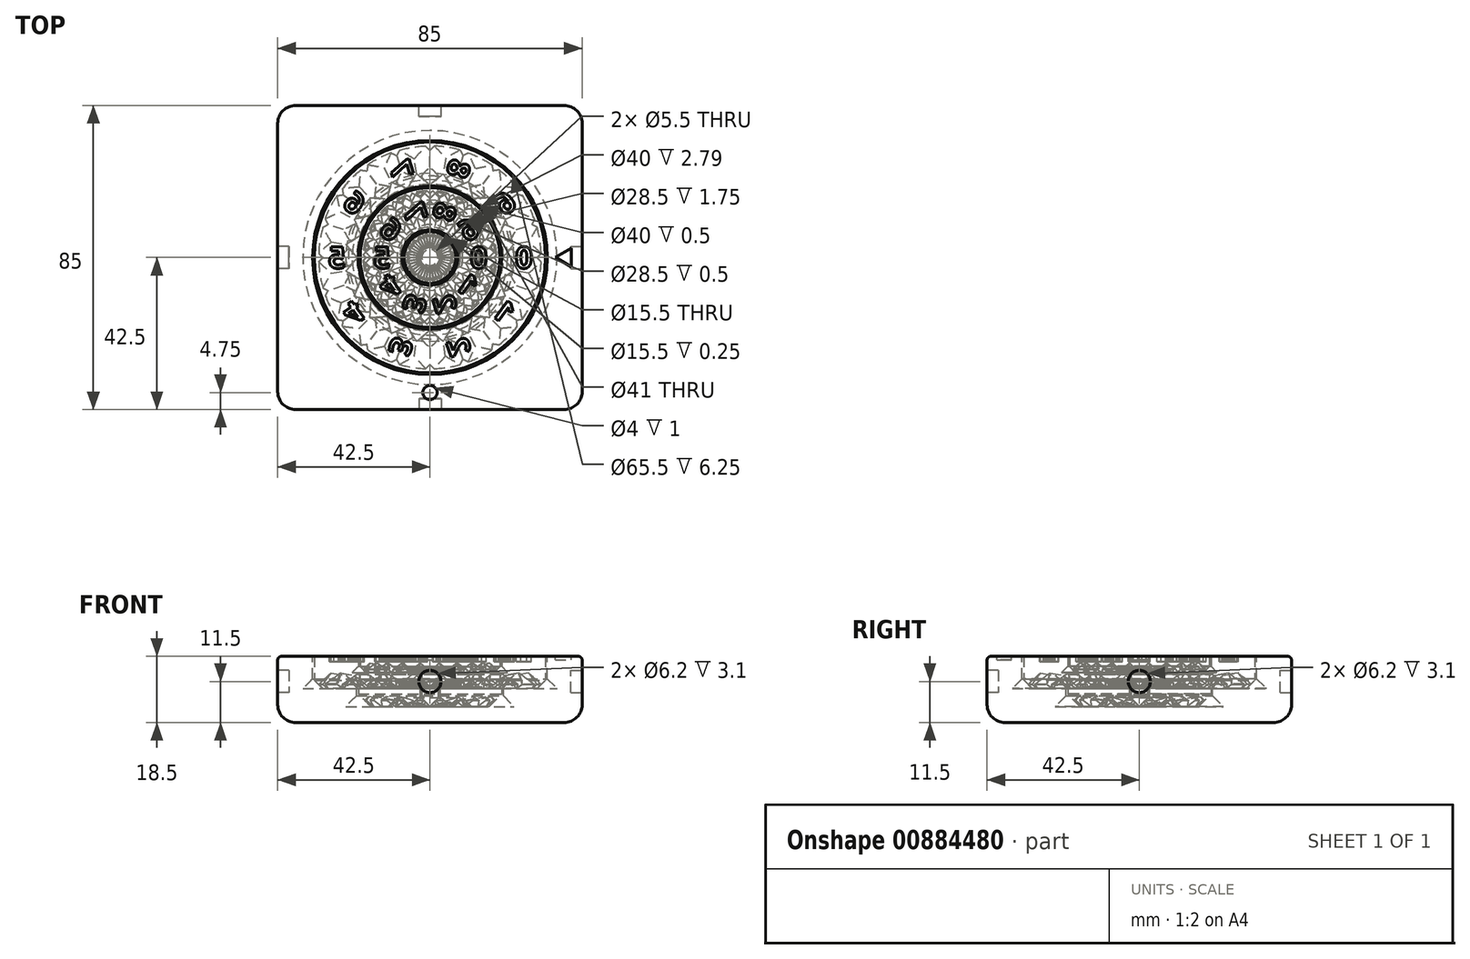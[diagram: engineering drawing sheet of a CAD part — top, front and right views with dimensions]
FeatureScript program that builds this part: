
annotation { "Feature Type Name" : "Feature", "Feature Type Description" : "" }
export const myFeature = defineFeature(function(context is Context, id is Id, definition is map)
    precondition{}
    {
        {
            var Q0;
            Q0=qCreatedBy(makeId("Top.planeOp"),FACE);
            var sketch = newSketch(context, id + "F0", { "sketchPlane" : qUnion([Q0])});
            skLineSegment(sketch, "E0.bottom", {"start": v(-42.5, 42.5) * mm, "end": v(42.5, 42.5) * mm});
            skLineSegment(sketch, "E0.top", {"start": v(-42.5, -42.5) * mm, "end": v(42.5, -42.5) * mm});
            skLineSegment(sketch, "E0.left", {"start": v(-42.5, 42.5) * mm, "end": v(-42.5, -42.5) * mm});
            skLineSegment(sketch, "E0.right", {"start": v(42.5, 42.5) * mm, "end": v(42.5, -42.5) * mm});
            skLineSegment(sketch, "E1", {"start": v(-42.5, 0) * mm, "end": v(42.5, 0) * mm, "construction": true});
            skLineSegment(sketch, "E2", {"start": v(0, -42.5) * mm, "end": v(0, 42.5) * mm, "construction": true});
            skCircle(sketch, "E3", {"center": v(0, -37.75) * mm, "radius": 2 * mm});
            skCircle(sketch, "E4", {"center": v(0, 0) * mm, "radius": 32.75 * mm});
            skCircle(sketch, "E5", {"center": v(0, 0) * mm, "radius": 20.5 * mm});
            skSolve(sketch);
        }
        {
            assignVariable(context, id + "F1", {"name" : "h", "anyValue" : 18.5});
        }
        {
            assignVariable(context, id + "F2", {"name" : "d", "anyValue" : 14});
        }
        {
            var Q0;
            Q0=makeQuery(id+"F0.imprint","IMPRINT",FACE,{"disambiguationData":[TD([[makeQuery(id+"F0.imprint","IMPRINT",EDGE,{"derivedFrom":sQuery(id+"F0.wireOp",EDGE,"TAnjNuv1-8zZz-IdIO-9YnW-rZbYslCo22iK.bottom")}),-1.0]])]});
            var Q1;
            Q1=makeQuery(id+"F0.imprint","IMPRINT",FACE,{"disambiguationData":[TD([[makeQuery(id+"F0.imprint","IMPRINT",EDGE,{"derivedFrom":sQuery(id+"F0.wireOp",EDGE,"E0.bottom")}),-1.0]])]});
            var Q2;
            Q2=makeQuery(id+"F0.imprint","IMPRINT",FACE,{"disambiguationData":[TD([[makeQuery(id+"F0.imprint","IMPRINT",EDGE,{"derivedFrom":sQuery(id+"F0.wireOp",EDGE,"2ee7e992-b2ee-4d81-b33c-59d4d4482344.0.2.0")}),1.0]])]});
            var Q3;
            Q3=makeQuery(id+"F0.imprint","IMPRINT",FACE,{"disambiguationData":[TD([[makeQuery(id+"F0.imprint","IMPRINT",EDGE,{"derivedFrom":sQuery(id+"F0.wireOp",EDGE,"2ee7e992-b2ee-4d81-b33c-59d4d4482344.0.3.0")}),1.0]])]});
            var Q4;
            Q4=makeQuery(id+"F0.imprint","IMPRINT",FACE,{"disambiguationData":[TD([[makeQuery(id+"F0.imprint","IMPRINT",EDGE,{"derivedFrom":sQuery(id+"F0.wireOp",EDGE,"2ee7e992-b2ee-4d81-b33c-59d4d4482344.0.1.0")}),1.0]])]});
            var Q5;
            Q5=makeQuery(id+"F0.imprint","IMPRINT",FACE,{"disambiguationData":[TD([[makeQuery(id+"F0.imprint","IMPRINT",EDGE,{"derivedFrom":sQuery(id+"F0.wireOp",EDGE,"f406dc69-17c4-4892-9ae8-b8d3958ef0eb.0.1.2")}),1.0]])]});
            var Q6;
            Q6=makeQuery(id+"F0.imprint","IMPRINT",FACE,{"disambiguationData":[TD([[makeQuery(id+"F0.imprint","IMPRINT",EDGE,{"derivedFrom":sQuery(id+"F0.wireOp",EDGE,"f406dc69-17c4-4892-9ae8-b8d3958ef0eb.0.2.2")}),1.0]])]});
            var Q7;
            Q7=makeQuery(id+"F0.imprint","IMPRINT",FACE,{"disambiguationData":[TD([[makeQuery(id+"F0.imprint","IMPRINT",EDGE,{"derivedFrom":sQuery(id+"F0.wireOp",EDGE,"f406dc69-17c4-4892-9ae8-b8d3958ef0eb.0.3.2")}),1.0]])]});
            var Q8;
            Q8=makeQuery(id+"F0.imprint","IMPRINT",FACE,{"disambiguationData":[TD([[makeQuery(id+"F0.imprint","IMPRINT",EDGE,{"derivedFrom":sQuery(id+"F0.wireOp",EDGE,"E3")}),1.0]])]});
            var Q9;
            Q9=makeQuery(id+"F0.imprint","IMPRINT",FACE,{"disambiguationData":[TD([[makeQuery(id+"F0.imprint","IMPRINT",EDGE,{"derivedFrom":sQuery(id+"F0.wireOp",EDGE,"E4")}),1.0]])]});
            var Q10;
            Q10=makeQuery(id+"F0.imprint","IMPRINT",FACE,{"disambiguationData":[TD([[makeQuery(id+"F0.imprint","IMPRINT",EDGE,{"derivedFrom":sQuery(id+"F0.wireOp",EDGE,"E5")}),1.0]])]});
            extrude(context, id + "F3", {"entities" : qUnion([Q0, Q1, Q2, Q3, Q4, Q5, Q6, Q7, Q8, Q9, Q10]), "depth" : (getVariable(context, 'h')) * mm, "offsetDistance" : 25 * mm});
        }
        {
            var Q0;
            Q0=makeQuery(id+"F0.imprint","IMPRINT",FACE,{"disambiguationData":[TD([[makeQuery(id+"F0.imprint","IMPRINT",EDGE,{"derivedFrom":sQuery(id+"F0.wireOp",EDGE,"E4")}),1.0]])]});
            extrude(context, id + "F4", {"entities" : qUnion([Q0]), "operationType" : NewBodyOperationType.REMOVE, "depth" : (getVariable(context, 'd') - 5) * mm, "offsetDistance" : 25 * mm});
        }
        {
            var Q0;
            Q0=makeQuery(id+"F0.imprint","IMPRINT",FACE,{"disambiguationData":[TD([[makeQuery(id+"F0.imprint","IMPRINT",EDGE,{"derivedFrom":sQuery(id+"F0.wireOp",EDGE,"E5")}),1.0]])]});
            extrude(context, id + "F5", {"entities" : qUnion([Q0]), "operationType" : NewBodyOperationType.REMOVE, "depth" : (getVariable(context, 'd')) * mm, "offsetDistance" : 25 * mm});
        }
        {
            var Q0;
            Q0=makeQuery(id+"F3.opExtrude","CAP_FACE",FACE,{"disambiguationData":[OSD([sQuery(id+"F0.wireOp",EDGE,"E0.bottom"),sQuery(id+"F0.wireOp",EDGE,"E0.top"),sQuery(id+"F0.wireOp",EDGE,"E0.left"),sQuery(id+"F0.wireOp",EDGE,"E0.right")])],"isStart":false});
            var Q1;
            Q1=makeQuery(id+"F3.opExtrude","SWEPT_EDGE",EDGE,{"disambiguationData":[OSD([sQuery(id+"F0.wireOp",EDGE,"E0.bottom"),sQuery(id+"F0.wireOp",EDGE,"E0.right")])]});
            var Q2;
            Q2=makeQuery(id+"F3.opExtrude","SWEPT_EDGE",EDGE,{"disambiguationData":[OSD([sQuery(id+"F0.wireOp",EDGE,"E0.bottom"),sQuery(id+"F0.wireOp",EDGE,"E0.left")])]});
            var Q3;
            Q3=makeQuery(id+"F3.opExtrude","SWEPT_EDGE",EDGE,{"disambiguationData":[OSD([sQuery(id+"F0.wireOp",EDGE,"E0.top"),sQuery(id+"F0.wireOp",EDGE,"E0.left")])]});
            var Q4;
            Q4=makeQuery(id+"F3.opExtrude","SWEPT_EDGE",EDGE,{"disambiguationData":[OSD([sQuery(id+"F0.wireOp",EDGE,"E0.top"),sQuery(id+"F0.wireOp",EDGE,"E0.right")])]});
            fillet(context, id + "F6", {"entities" : qUnion([Q0, Q1, Q2, Q3, Q4]), "radius" : 5 * mm, "tangentPropagation" : true, "allowEdgeOverflow" : false});
        }
        {
            var Q0;
            Q0=makeQuery(id+"F3.opExtrude","CAP_EDGE",EDGE,{"disambiguationData":[OSD([sQuery(id+"F0.wireOp",EDGE,"E0.left")])],"isStart":true});
            fillet(context, id + "F7", {"entities" : qUnion([Q0]), "radius" : 1 * mm, "tangentPropagation" : true, "allowEdgeOverflow" : false});
        }
        {
            var Q0;
            Q0=makeQuery(id+"F3.opExtrude","SWEPT_FACE",FACE,{"disambiguationData":[OSD([sQuery(id+"F0.wireOp",EDGE,"E0.top")])]});
            var sketch = newSketch(context, id + "F8", { "sketchPlane" : qUnion([Q0])});
            skCircle(sketch, "E6", {"center": v(0, 7) * mm, "radius": 3.1 * mm});
            skSolve(sketch);
        }
        {
            var Q0;
            Q0=makeQuery(id+"F8.imprint","IMPRINT",FACE,{"disambiguationData":[TD([[makeQuery(id+"F8.imprint","IMPRINT",EDGE,{"derivedFrom":sQuery(id+"F8.wireOp",EDGE,"E6")}),1.0]])]});
            extrude(context, id + "F9", {"entities" : qUnion([Q0]), "operationType" : NewBodyOperationType.REMOVE, "oppositeDirection" : true, "depth" : 3.1 * mm, "offsetDistance" : 25 * mm});
        }
        {
            var Q0;
            Q0=makeQuery(id+"F3.opExtrude","SWEPT_FACE",FACE,{"disambiguationData":[OSD([sQuery(id+"F0.wireOp",EDGE,"E0.bottom")])]});
            var sketch = newSketch(context, id + "F10", { "sketchPlane" : qUnion([Q0])});
            skCircle(sketch, "E7", {"center": v(0, 7) * mm, "radius": 3.1 * mm});
            skSolve(sketch);
        }
        {
            var Q0;
            Q0=makeQuery(id+"F10.imprint","IMPRINT",FACE,{"disambiguationData":[TD([[makeQuery(id+"F10.imprint","IMPRINT",EDGE,{"derivedFrom":sQuery(id+"F10.wireOp",EDGE,"E7")}),1.0]])]});
            extrude(context, id + "F11", {"entities" : qUnion([Q0]), "operationType" : NewBodyOperationType.REMOVE, "oppositeDirection" : true, "depth" : 3.1 * mm, "offsetDistance" : 25 * mm});
        }
        {
            var Q0;
            Q0=makeQuery(id+"F3.opExtrude","SWEPT_FACE",FACE,{"disambiguationData":[OSD([sQuery(id+"F0.wireOp",EDGE,"E0.left")])]});
            var sketch = newSketch(context, id + "F12", { "sketchPlane" : qUnion([Q0])});
            skCircle(sketch, "E8", {"center": v(0, 7) * mm, "radius": 3.1 * mm});
            skSolve(sketch);
        }
        {
            var Q0;
            Q0=makeQuery(id+"F12.imprint","IMPRINT",FACE,{"disambiguationData":[TD([[makeQuery(id+"F12.imprint","IMPRINT",EDGE,{"derivedFrom":sQuery(id+"F12.wireOp",EDGE,"E8")}),1.0]])]});
            extrude(context, id + "F13", {"entities" : qUnion([Q0]), "operationType" : NewBodyOperationType.REMOVE, "oppositeDirection" : true, "depth" : 3.1 * mm, "offsetDistance" : 25 * mm});
        }
        {
            var Q0;
            Q0=makeQuery(id+"F3.opExtrude","SWEPT_FACE",FACE,{"disambiguationData":[OSD([sQuery(id+"F0.wireOp",EDGE,"E0.right")])]});
            var sketch = newSketch(context, id + "F14", { "sketchPlane" : qUnion([Q0])});
            skCircle(sketch, "E9", {"center": v(0, 7) * mm, "radius": 3.1 * mm});
            skSolve(sketch);
        }
        {
            var Q0;
            Q0=makeQuery(id+"F14.imprint","IMPRINT",FACE,{"disambiguationData":[TD([[makeQuery(id+"F14.imprint","IMPRINT",EDGE,{"derivedFrom":sQuery(id+"F14.wireOp",EDGE,"E9")}),1.0]])]});
            extrude(context, id + "F15", {"entities" : qUnion([Q0]), "operationType" : NewBodyOperationType.REMOVE, "oppositeDirection" : true, "depth" : 3.1 * mm, "offsetDistance" : 25 * mm});
        }
        {
            var Q0;
            Q0=makeQuery(id+"F0.imprint","IMPRINT",FACE,{"disambiguationData":[TD([[makeQuery(id+"F0.imprint","IMPRINT",EDGE,{"derivedFrom":sQuery(id+"F0.wireOp",EDGE,"E3")}),1.0]])]});
            var Q1;
            Q1=sQuery(id+"F0.wireOp",EDGE,"E3");
            extrude(context, id + "F16", {"entities" : qUnion([Q0]), "operationType" : NewBodyOperationType.REMOVE, "surfaceEntities" : qUnion([Q1]), "depth" : 1 * mm, "offsetDistance" : 25 * mm});
        }
        {
            var Q0;
            Q0=qCreatedBy(makeId("Front.planeOp"),FACE);
            var sketch = newSketch(context, id + "F17", { "sketchPlane" : qUnion([Q0])});
            skLineSegment(sketch, "E10", {"start": v(0, 14) * mm, "end": v(0, 9) * mm, "construction": true});
            skLineSegment(sketch, "E11", {"start": v(-20, 0) * mm, "end": v(-32.25, 0) * mm});
            skLineSegment(sketch, "E12", {"start": v(-32.25, 0) * mm, "end": v(-32.25, 9) * mm});
            skLineSegment(sketch, "E13", {"start": v(-32.25, 9) * mm, "end": v(-20, 9) * mm});
            skLineSegment(sketch, "E14", {"start": v(-20, 9) * mm, "end": v(-20, 14) * mm});
            skLineSegment(sketch, "E15", {"start": v(-20, 14) * mm, "end": v(-2.75, 14) * mm});
            skPoint(sketch, "E16.visualSharp", {"position": v(-20, 14) * mm});
            skPoint(sketch, "E17.visualSharp", {"position": v(-32.25, 9) * mm});
            skPoint(sketch, "E18.visualSharp", {"position": v(-20, 9) * mm});
            skPoint(sketch, "E19.orphan", {"position": v(0, 28.15) * mm});
            skLineSegment(sketch, "E20", {"start": v(-20, 0) * mm, "end": v(-20, 5) * mm});
            skLineSegment(sketch, "E21", {"start": v(-20, 5) * mm, "end": v(-14.25, 5) * mm});
            skLineSegment(sketch, "E22", {"start": v(-14.25, 5) * mm, "end": v(-14.25, 9) * mm});
            skLineSegment(sketch, "E23", {"start": v(-14.25, 9) * mm, "end": v(-2.75, 9) * mm});
            skPoint(sketch, "E24.visualSharp", {"position": v(-14.25, 9) * mm});
            skPoint(sketch, "E25.visualSharp", {"position": v(-14.25, 5) * mm});
            skPoint(sketch, "E26.visualSharp", {"position": v(-20, 5) * mm});
            skLineSegment(sketch, "E27", {"start": v(-2.75, 14) * mm, "end": v(-2.75, 9) * mm});
            skSolve(sketch);
        }
        {
            var Q0;
            Q0=makeQuery(id+"F17.imprint","IMPRINT",FACE,{"disambiguationData":[TD([[makeQuery(id+"F17.imprint","IMPRINT",EDGE,{"derivedFrom":sQuery(id+"F17.wireOp",EDGE,"E11")}),-1.0]])]});
            var Q1;
            Q1 = qConstructionFilter(qBodyType(qCreatedBy(id + "F17" ,EDGE), BodyType.WIRE), ConstructionObject.NO);
            var Q2;
            Q2=sQuery(id+"F17.wireOp",EDGE,"E10");
            revolve(context, id + "F18", {"surfaceOperationType" : NewSurfaceOperationType.NEW, "entities" : qUnion([Q0]), "surfaceEntities" : qUnion([Q1]), "axis" : qUnion([Q2]), "revolveType" : RevolveType.FULL});
        }
        {
            var Q0;
            Q0=qCreatedBy(makeId("Front.planeOp"),FACE);
            var sketch = newSketch(context, id + "F19", { "sketchPlane" : qUnion([Q0])});
            skLineSegment(sketch, "E28", {"start": v(-2.75, 8.5) * mm, "end": v(-13.75, 8.5) * mm});
            skLineSegment(sketch, "E29", {"start": v(-13.75, 8.5) * mm, "end": v(-13.75, 4.5) * mm});
            skLineSegment(sketch, "E30", {"start": v(-13.75, 4.5) * mm, "end": v(-19.5, 4.5) * mm});
            skLineSegment(sketch, "E31", {"start": v(-19.5, 4.5) * mm, "end": v(-19.5, 0) * mm});
            skLineSegment(sketch, "E32", {"start": v(-19.5, 0) * mm, "end": v(-7.75, 0) * mm});
            skLineSegment(sketch, "E33", {"start": v(-7.75, 0) * mm, "end": v(-7.75, 4.5) * mm});
            skLineSegment(sketch, "E34", {"start": v(-7.75, 4.5) * mm, "end": v(-2.75, 4.5) * mm});
            skLineSegment(sketch, "E35", {"start": v(-2.75, 4.5) * mm, "end": v(-2.75, 8.5) * mm});
            skPoint(sketch, "E36.orphan", {"position": v(0, 8.5) * mm});
            skLineSegment(sketch, "E37", {"start": v(0, 19.44) * mm, "end": v(0, -7.38) * mm, "construction": true});
            skSolve(sketch);
        }
        {
            var Q0;
            Q0=makeQuery(id+"F19.imprint","IMPRINT",FACE,{"disambiguationData":[TD([[makeQuery(id+"F19.imprint","IMPRINT",EDGE,{"derivedFrom":sQuery(id+"F19.wireOp",EDGE,"E28")}),1.0]])]});
            var Q1;
            Q1=sQuery(id+"F19.wireOp",EDGE,"E37");
            revolve(context, id + "F20", {"surfaceOperationType" : NewSurfaceOperationType.NEW, "entities" : qUnion([Q0]), "axis" : qUnion([Q1]), "revolveType" : RevolveType.FULL});
        }
        {
            var Q0;
            Q0=makeQuery(id+"F0.imprint","IMPRINT",FACE,{"disambiguationData":[TD([[makeQuery(id+"F0.imprint","IMPRINT",EDGE,{"derivedFrom":sQuery(id+"F0.wireOp",EDGE,"E0.bottom")}),-1.0]])]});
            var sketch = newSketch(context, id + "F21", { "sketchPlane" : qUnion([Q0])});
            skLineSegment(sketch, "E38", {"start": v(0, 0) * mm, "end": v(13.5, 0) * mm, "construction": true});
            skLineSegment(sketch, "E39.1.0", {"start": v(0, 0) * mm, "end": v(32.76, 23.8) * mm, "construction": true});
            skLineSegment(sketch, "E39.2.0", {"start": v(0, 0) * mm, "end": v(12.51, 38.5) * mm, "construction": true});
            skLineSegment(sketch, "E39.3.0", {"start": v(0, 0) * mm, "end": v(-12.51, 38.5) * mm, "construction": true});
            skLineSegment(sketch, "E39.4.0", {"start": v(0, 0) * mm, "end": v(-32.76, 23.8) * mm, "construction": true});
            skLineSegment(sketch, "E39.5.0", {"start": v(0, 0) * mm, "end": v(-13.5, 0) * mm, "construction": true});
            skLineSegment(sketch, "E39.6.0", {"start": v(0, 0) * mm, "end": v(-21.14, -15.36) * mm, "construction": true});
            skLineSegment(sketch, "E39.7.0", {"start": v(0, 0) * mm, "end": v(-12.51, -38.5) * mm, "construction": true});
            skLineSegment(sketch, "E39.8.0", {"start": v(0, 0) * mm, "end": v(8.07, -24.85) * mm, "construction": true});
            skLineSegment(sketch, "E39.9.0", {"start": v(0, 0) * mm, "end": v(21.14, -15.36) * mm, "construction": true});
            skPoint(sketch, "E39.center", {"position": v(0, 0) * mm});
            skCircle(sketch, "E40", {"center": v(0, 0) * mm, "radius": 32.5 * mm, "construction": true});
            skCircle(sketch, "E41", {"center": v(0, 0) * mm, "radius": 19.75 * mm, "construction": true});
            skText(sketch, "E42", { "text": "0", "fontName": "OpenSans-Bold.ttf"});
            skLineSegment(sketch, "E43", {"start": v(-26.12, 0) * mm, "end": v(-28.62, 0) * mm, "construction": true});
            skLineSegment(sketch, "E44", {"start": v(-21.14, -15.36) * mm, "end": v(-32.76, -23.8) * mm, "construction": true});
            skArc(sketch, "E45", {"start": v(-21.14, 15.36) * mm, "mid": v(-24.85, -8.07) * mm, "end": v(-8.07, -24.85) * mm, "construction": true});
            skArc(sketch, "E46", {"start": v(-8.07, 24.85) * mm, "mid": v(-15.36, 21.14) * mm, "end": v(-21.14, 15.36) * mm, "construction": true});
            skArc(sketch, "E47", {"start": v(8.07, 24.85) * mm, "mid": v(0, 26.12) * mm, "end": v(-8.07, 24.85) * mm, "construction": true});
            skArc(sketch, "E48", {"start": v(21.14, 15.36) * mm, "mid": v(15.36, 21.14) * mm, "end": v(8.07, 24.85) * mm, "construction": true});
            skArc(sketch, "E49", {"start": v(26.12, 0) * mm, "mid": v(24.85, 8.07) * mm, "end": v(21.14, 15.36) * mm, "construction": true});
            skLineSegment(sketch, "E50", {"start": v(21.14, -15.36) * mm, "end": v(32.76, -23.8) * mm, "construction": true});
            skLineSegment(sketch, "E51", {"start": v(8.07, -24.85) * mm, "end": v(12.51, -38.5) * mm, "construction": true});
            skArc(sketch, "E52", {"start": v(-8.07, -24.85) * mm, "mid": v(15.36, -21.14) * mm, "end": v(26.12, 0) * mm, "construction": true});
            skText(sketch, "E53", { "text": "1", "fontName": "OpenSans-Bold.ttf"});
            skLineSegment(sketch, "E54", {"start": v(-21.14, -15.36) * mm, "end": v(-22.75, -16.53) * mm, "construction": true});
            skText(sketch, "E55", { "text": "2", "fontName": "OpenSans-Bold.ttf"});
            skLineSegment(sketch, "E56", {"start": v(-8.07, -24.85) * mm, "end": v(-8.85, -27.24) * mm, "construction": true});
            skText(sketch, "E57", { "text": "3", "fontName": "OpenSans-Bold.ttf"});
            skLineSegment(sketch, "E58", {"start": v(8.07, -24.85) * mm, "end": v(8.84, -27.21) * mm, "construction": true});
            skText(sketch, "E59", { "text": "4", "fontName": "OpenSans-Bold.ttf"});
            skLineSegment(sketch, "E60", {"start": v(23.23, -16.87) * mm, "end": v(21.14, -15.36) * mm, "construction": true});
            skText(sketch, "E61", { "text": "5\n", "fontName": "OpenSans-Bold.ttf"});
            skLineSegment(sketch, "E62", {"start": v(26.13, 0) * mm, "end": v(23.66, 0) * mm, "construction": true});
            skText(sketch, "E63", { "text": "6\n", "fontName": "OpenSans-Bold.ttf"});
            skLineSegment(sketch, "E64", {"start": v(21.14, 15.36) * mm, "end": v(23.17, 16.83) * mm, "construction": true});
            skText(sketch, "E65", { "text": "7", "fontName": "OpenSans-Bold.ttf"});
            skLineSegment(sketch, "E66", {"start": v(8.07, 24.85) * mm, "end": v(8.85, 27.24) * mm, "construction": true});
            skText(sketch, "E67", { "text": "8", "fontName": "OpenSans-Bold.ttf"});
            skLineSegment(sketch, "E68", {"start": v(-8.85, 27.23) * mm, "end": v(-8.07, 24.85) * mm, "construction": true});
            skText(sketch, "E69", { "text": "9", "fontName": "OpenSans-Bold.ttf"});
            skLineSegment(sketch, "E70", {"start": v(-23.16, 16.83) * mm, "end": v(-21.14, 15.36) * mm, "construction": true});
            skText(sketch, "E71", { "text": "5\n", "fontName": "OpenSans-Bold.ttf"});
            skLineSegment(sketch, "E72", {"start": v(13.5, 0) * mm, "end": v(11.04, 0) * mm, "construction": true});
            skCircle(sketch, "E73", {"center": v(0, 0) * mm, "radius": 7.5 * mm, "construction": true});
            skCircle(sketch, "E74", {"center": v(0, 0) * mm, "radius": 19.5 * mm, "construction": true});
            skLineSegment(sketch, "E75", {"start": v(13.5, 0) * mm, "end": v(40.49, 0) * mm, "construction": true});
            skArc(sketch, "E76", {"start": v(10.92, 7.94) * mm, "mid": v(7.94, 10.92) * mm, "end": v(4.17, 12.84) * mm, "construction": true});
            skArc(sketch, "E77", {"start": v(10.92, -7.94) * mm, "mid": v(13.5, 0) * mm, "end": v(10.92, 7.94) * mm, "construction": true});
            skArc(sketch, "E78", {"start": v(4.17, -12.84) * mm, "mid": v(7.94, -10.92) * mm, "end": v(10.92, -7.94) * mm, "construction": true});
            skArc(sketch, "E79", {"start": v(-4.17, -12.84) * mm, "mid": v(0, -13.5) * mm, "end": v(4.17, -12.84) * mm, "construction": true});
            skArc(sketch, "E80", {"start": v(4.17, 12.84) * mm, "mid": v(0, 13.5) * mm, "end": v(-4.17, 12.84) * mm, "construction": true});
            skArc(sketch, "E81", {"start": v(-4.17, 12.84) * mm, "mid": v(-7.94, 10.92) * mm, "end": v(-10.92, 7.94) * mm, "construction": true});
            skArc(sketch, "E82", {"start": v(-10.92, 7.94) * mm, "mid": v(-13.5, 0) * mm, "end": v(-10.92, -7.94) * mm, "construction": true});
            skLineSegment(sketch, "E83", {"start": v(-13.5, 0) * mm, "end": v(-40.49, 0) * mm, "construction": true});
            skArc(sketch, "E84", {"start": v(-10.92, -7.94) * mm, "mid": v(-7.94, -10.92) * mm, "end": v(-4.17, -12.84) * mm, "construction": true});
            skText(sketch, "E85", { "text": "6\n", "fontName": "OpenSans-Bold.ttf"});
            skLineSegment(sketch, "E86", {"start": v(10.92, 7.94) * mm, "end": v(12.96, 9.41) * mm, "construction": true});
            skText(sketch, "E87", { "text": "7", "fontName": "OpenSans-Bold.ttf"});
            skLineSegment(sketch, "E88", {"start": v(4.17, 12.84) * mm, "end": v(4.95, 15.23) * mm, "construction": true});
            skText(sketch, "E89", { "text": "8", "fontName": "OpenSans-Bold.ttf"});
            skLineSegment(sketch, "E90", {"start": v(-4.95, 15.22) * mm, "end": v(-4.17, 12.84) * mm, "construction": true});
            skText(sketch, "E91", { "text": "9", "fontName": "OpenSans-Bold.ttf"});
            skLineSegment(sketch, "E92", {"start": v(-12.95, 9.4) * mm, "end": v(-10.92, 7.94) * mm, "construction": true});
            skText(sketch, "E93", { "text": "0", "fontName": "OpenSans-Bold.ttf"});
            skLineSegment(sketch, "E94", {"start": v(-13.5, 0) * mm, "end": v(-16, 0) * mm, "construction": true});
            skText(sketch, "E95", { "text": "1", "fontName": "OpenSans-Bold.ttf"});
            skLineSegment(sketch, "E96", {"start": v(-10.92, -7.94) * mm, "end": v(-12.53, -9.1) * mm, "construction": true});
            skText(sketch, "E97", { "text": "2", "fontName": "OpenSans-Bold.ttf"});
            skLineSegment(sketch, "E98", {"start": v(-4.17, -12.84) * mm, "end": v(-4.95, -15.23) * mm, "construction": true});
            skText(sketch, "E99", { "text": "3", "fontName": "OpenSans-Bold.ttf"});
            skLineSegment(sketch, "E100", {"start": v(4.17, -12.84) * mm, "end": v(4.94, -15.2) * mm, "construction": true});
            skText(sketch, "E101", { "text": "4", "fontName": "OpenSans-Bold.ttf"});
            skLineSegment(sketch, "E102", {"start": v(13.01, -9.45) * mm, "end": v(10.92, -7.94) * mm, "construction": true});
            const initialGuessF21  = {"E42": [-0.02862, -0.003, 1, 0, 0.006], "E53": [-0.02098, -0.01895, 0.80902, 0.58779, 0.006], "E55": [-0.006, -0.02817, 0.30902, 0.95106, 0.006], "E57": [0.0117, -0.02629, -0.30902, 0.95106, 0.006], "E59": [0.02499, -0.01445, -0.80902, 0.58779, 0.006], "E61": [0.02366, -0.003, 1, 0, 0.006], "E63": [0.02086, 0.01145, 0.80902, 0.58779, 0.006], "E65": [0.01015, 0.02153, 0.30902, 0.95106, 0.006], "E67": [-0.00445, 0.0234, -0.30902, 0.95106, 0.006], "E69": [-0.01735, 0.01631, -0.80902, 0.58779, 0.006], "E71": [0.01104, -0.003, 1, 0, 0.006], "E85": [0.01065, 0.00403, 0.80902, 0.58779, 0.006], "E87": [0.00625, 0.00952, 0.30902, 0.95106, 0.006], "E89": [-0.00054, 0.01138, -0.30902, 0.95106, 0.006], "E91": [-0.00713, 0.0089, -0.80902, 0.58779, 0.006], "E93": [-0.016, -0.003, 1, 0, 0.006], "E95": [-0.01077, -0.01153, 0.80902, 0.58779, 0.006], "E97": [-0.0021, -0.01616, 0.30902, 0.95106, 0.006], "E99": [0.0078, -0.01428, -0.30902, 0.95106, 0.006], "E101": [0.01478, -0.00703, -0.80902, 0.58779, 0.006]};
            skSetInitialGuess(sketch, initialGuessF21);
            skSolve(sketch);
        }
        {
            var Q0;
            Q0 = qSketchRegion(id + "F21", true);
            extrude(context, id + "F22", {"entities" : qUnion([Q0]), "operationType" : NewBodyOperationType.REMOVE, "depth" : 1.5 * mm, "offsetDistance" : 25 * mm});
        }
        {
            var Q0;
            Q0 = qSketchRegion(id + "F21", true);
            extrude(context, id + "F23", {"entities" : qUnion([Q0]), "operationType" : NewBodyOperationType.REMOVE, "depth" : 1.5 * mm, "offsetDistance" : 25 * mm});
        }
        {
            var Q0;
            Q0=qCreatedBy(makeId("Front.planeOp"),FACE);
            var sketch = newSketch(context, id + "F24", { "sketchPlane" : qUnion([Q0])});
            skLineSegment(sketch, "E103", {"start": v(0, 0) * mm, "end": v(7.25, 0) * mm});
            skLineSegment(sketch, "E104", {"start": v(7.25, 0) * mm, "end": v(7.25, 4.25) * mm});
            skLineSegment(sketch, "E105", {"start": v(7.25, 4.25) * mm, "end": v(2.25, 4.25) * mm});
            skLineSegment(sketch, "E106", {"start": v(2.25, 4.25) * mm, "end": v(2.25, 18.5) * mm});
            skLineSegment(sketch, "E107", {"start": v(2.25, 18.5) * mm, "end": v(0, 18.5) * mm});
            skLineSegment(sketch, "E108", {"start": v(0, 18.5) * mm, "end": v(0, 0) * mm});
            skSolve(sketch);
        }
        {
            var Q0;
            Q0=makeQuery(id+"F24.imprint","IMPRINT",FACE,{"disambiguationData":[TD([[makeQuery(id+"F24.imprint","IMPRINT",EDGE,{"derivedFrom":sQuery(id+"F24.wireOp",EDGE,"E103")}),1.0]])]});
            var Q1;
            Q1=sQuery(id+"F24.wireOp",EDGE,"E108");
            revolve(context, id + "F25", {"operationType" : NewBodyOperationType.ADD, "surfaceOperationType" : NewSurfaceOperationType.NEW, "entities" : qUnion([Q0]), "axis" : qUnion([Q1]), "revolveType" : RevolveType.FULL});
        }
        {
            var Q0;
            Q0=makeQuery(id+"F3.opExtrude","SWEPT_BODY",BODY,{"disambiguationData":[OSD([sQuery(id+"F0.wireOp",EDGE,"E0.bottom"),sQuery(id+"F0.wireOp",EDGE,"E0.top"),sQuery(id+"F0.wireOp",EDGE,"E0.left"),sQuery(id+"F0.wireOp",EDGE,"E0.right")])]});
            var Q1;
            Q1=makeQuery(id+"F18.opRevolve","SWEPT_BODY",BODY,{"disambiguationData":[OSD([sQuery(id+"F17.wireOp",EDGE,"E11"),sQuery(id+"F17.wireOp",EDGE,"E12"),sQuery(id+"F17.wireOp",EDGE,"E13"),sQuery(id+"F17.wireOp",EDGE,"E14"),sQuery(id+"F17.wireOp",EDGE,"E15"),sQuery(id+"F17.wireOp",EDGE,"E16.filletArc"),sQuery(id+"F17.wireOp",EDGE,"E17.filletArc"),sQuery(id+"F17.wireOp",EDGE,"E18.filletArc"),sQuery(id+"F17.wireOp",EDGE,"E20"),sQuery(id+"F17.wireOp",EDGE,"E21"),sQuery(id+"F17.wireOp",EDGE,"E22"),sQuery(id+"F17.wireOp",EDGE,"E23"),sQuery(id+"F17.wireOp",EDGE,"E24.filletArc"),sQuery(id+"F17.wireOp",EDGE,"E25.filletArc"),sQuery(id+"F17.wireOp",EDGE,"E26.filletArc"),sQuery(id+"F17.wireOp",EDGE,"E27")])]});
            var Q2;
            Q2=makeQuery(id+"F20.opRevolve","SWEPT_BODY",BODY,{"disambiguationData":[OSD([sQuery(id+"F19.wireOp",EDGE,"E28"),sQuery(id+"F19.wireOp",EDGE,"E29"),sQuery(id+"F19.wireOp",EDGE,"E30"),sQuery(id+"F19.wireOp",EDGE,"E31"),sQuery(id+"F19.wireOp",EDGE,"E32"),sQuery(id+"F19.wireOp",EDGE,"E33"),sQuery(id+"F19.wireOp",EDGE,"E34"),sQuery(id+"F19.wireOp",EDGE,"E35"),sQuery(id+"F19.wireOp",EDGE,"caf7a765-5534-4870-827b-03466f1c99e3.filletArc"),sQuery(id+"F19.wireOp",EDGE,"dd2b0f7d-4639-499b-b715-159063f6e088.filletArc"),sQuery(id+"F19.wireOp",EDGE,"7f4fc2b8-c080-4429-a952-9433392ce116.filletArc"),sQuery(id+"F19.wireOp",EDGE,"d3ce06f0-3ce8-42c3-862a-95c5991aedac.filletArc")])]});
            var Q3;
            Q3=sQuery(id+"F0.wireOp",EDGE,"E2");
            var Q4;
            Q4=sQuery(id+"F0.wireOp",EDGE,"E2");
            transform(context, id + "F26", {"entities" : qUnion([Q0, Q1, Q2]), "transformType" : TransformType.ROTATION, "transformAxis" : qUnion([Q4]), "angle" : 180 * degree, "makeCopy" : false});
        }
        {
            var Q0;
            Q0=makeQuery(id+"F25.opRevolve","SWEPT_FACE",FACE,{"disambiguationData":[OSD([sQuery(id+"F24.wireOp",EDGE,"E105")])]});
            var sketch = newSketch(context, id + "F27", { "sketchPlane" : qUnion([Q0])});
            skCircle(sketch, "E109", {"center": v(0, 0) * mm, "radius": 3.62 * mm});
            skCircle(sketch, "E110", {"center": v(0, 0) * mm, "radius": 5.85 * mm});
            skCircle(sketch, "E111", {"center": v(0, 0) * mm, "radius": 8.5 * mm});
            skSolve(sketch);
        }
        {
            var Q0;
            Q0=makeQuery(id+"F18.opRevolve","SWEPT_FACE",FACE,{"disambiguationData":[OSD([sQuery(id+"F17.wireOp",EDGE,"E15")])]});
            var sketch = newSketch(context, id + "F28", { "sketchPlane" : qUnion([Q0])});
            skLineSegment(sketch, "E112", {"start": v(0, 0) * mm, "end": v(32.5, 0) * mm});
            skLineSegment(sketch, "E113.1.0", {"start": v(0, 0) * mm, "end": v(19.04, 6.18) * mm});
            skLineSegment(sketch, "E113.2.0", {"start": v(0, 0) * mm, "end": v(16.2, 11.76) * mm});
            skLineSegment(sketch, "E113.3.0", {"start": v(0, 0) * mm, "end": v(19.1, 26.3) * mm});
            skLineSegment(sketch, "E113.4.0", {"start": v(0, 0) * mm, "end": v(10.04, 30.9) * mm});
            skLineSegment(sketch, "E113.5.0", {"start": v(0, 0) * mm, "end": v(0, 32.5) * mm});
            skLineSegment(sketch, "E113.6.0", {"start": v(0, 0) * mm, "end": v(-10.04, 30.9) * mm});
            skLineSegment(sketch, "E113.7.0", {"start": v(0, 0) * mm, "end": v(-19.1, 26.3) * mm});
            skLineSegment(sketch, "E113.8.0", {"start": v(0, 0) * mm, "end": v(-26.3, 19.1) * mm});
            skLineSegment(sketch, "E113.9.0", {"start": v(0, 0) * mm, "end": v(-19.04, 6.18) * mm});
            skLineSegment(sketch, "E113.10.0", {"start": v(0, 0) * mm, "end": v(-32.5, 0) * mm});
            skLineSegment(sketch, "E113.11.0", {"start": v(0, 0) * mm, "end": v(-30.9, -10.04) * mm});
            skLineSegment(sketch, "E113.12.0", {"start": v(0, 0) * mm, "end": v(-16.2, -11.76) * mm});
            skLineSegment(sketch, "E113.13.0", {"start": v(0, 0) * mm, "end": v(-19.1, -26.3) * mm});
            skLineSegment(sketch, "E113.14.0", {"start": v(0, 0) * mm, "end": v(-6.18, -19.04) * mm});
            skLineSegment(sketch, "E113.15.0", {"start": v(0, 0) * mm, "end": v(0, -20.01) * mm});
            skLineSegment(sketch, "E113.16.0", {"start": v(0, 0) * mm, "end": v(6.18, -19.04) * mm});
            skLineSegment(sketch, "E113.17.0", {"start": v(0, 0) * mm, "end": v(19.1, -26.3) * mm});
            skLineSegment(sketch, "E113.18.0", {"start": v(0, 0) * mm, "end": v(16.2, -11.76) * mm});
            skLineSegment(sketch, "E113.19.0", {"start": v(0, 0) * mm, "end": v(30.9, -10.04) * mm});
            skPoint(sketch, "E113.center", {"position": v(0, 0) * mm});
            skCircle(sketch, "E114", {"center": v(0, 0) * mm, "radius": 32.5 * mm});
            skArc(sketch, "E115", {"start": v(-16.2, 11.76) * mm, "mid": v(-19.04, 6.18) * mm, "end": v(-20.01, 0) * mm});
            skArc(sketch, "E116", {"start": v(-11.76, 16.2) * mm, "mid": v(-14.15, 14.15) * mm, "end": v(-16.2, 11.76) * mm});
            skArc(sketch, "E117", {"start": v(-6.18, 19.04) * mm, "mid": v(-9.09, 17.83) * mm, "end": v(-11.76, 16.2) * mm});
            skArc(sketch, "E118", {"start": v(0, 20.01) * mm, "mid": v(-3.13, 19.77) * mm, "end": v(-6.18, 19.04) * mm});
            skArc(sketch, "E119", {"start": v(6.18, 19.04) * mm, "mid": v(3.13, 19.77) * mm, "end": v(0, 20.01) * mm});
            skArc(sketch, "E120", {"start": v(11.76, 16.2) * mm, "mid": v(9.09, 17.83) * mm, "end": v(6.18, 19.04) * mm});
            skLineSegment(sketch, "E121", {"start": v(16.2, 11.76) * mm, "end": v(26.3, 19.1) * mm});
            skLineSegment(sketch, "E122", {"start": v(19.04, 6.18) * mm, "end": v(30.9, 10.04) * mm});
            skArc(sketch, "E123", {"start": v(20.01, 0) * mm, "mid": v(17.83, 9.09) * mm, "end": v(11.76, 16.2) * mm});
            skArc(sketch, "E124", {"start": v(19.04, -6.18) * mm, "mid": v(19.77, -3.13) * mm, "end": v(20.01, 0) * mm});
            skLineSegment(sketch, "E125", {"start": v(16.2, -11.76) * mm, "end": v(26.3, -19.1) * mm});
            skArc(sketch, "E126", {"start": v(11.76, -16.2) * mm, "mid": v(16.2, -11.76) * mm, "end": v(19.04, -6.18) * mm});
            skLineSegment(sketch, "E127", {"start": v(6.18, -19.04) * mm, "end": v(10.04, -30.9) * mm});
            skLineSegment(sketch, "E128", {"start": v(0, -20.01) * mm, "end": v(0, -32.5) * mm});
            skLineSegment(sketch, "E129", {"start": v(-6.18, -19.04) * mm, "end": v(-10.04, -30.9) * mm});
            skArc(sketch, "E130", {"start": v(-11.76, -16.2) * mm, "mid": v(0, -20.01) * mm, "end": v(11.76, -16.2) * mm});
            skLineSegment(sketch, "E131", {"start": v(-16.2, -11.76) * mm, "end": v(-26.3, -19.1) * mm});
            skArc(sketch, "E132", {"start": v(-19.04, -6.18) * mm, "mid": v(-16.2, -11.76) * mm, "end": v(-11.76, -16.2) * mm});
            skArc(sketch, "E133", {"start": v(-20.01, 0) * mm, "mid": v(-19.77, -3.13) * mm, "end": v(-19.04, -6.18) * mm});
            skLineSegment(sketch, "E134", {"start": v(-19.04, 6.18) * mm, "end": v(-30.9, 10.04) * mm});
            skSolve(sketch);
        }
        {
            var Q0;
            Q0=makeQuery(id+"F18.opRevolve","SWEPT_FACE",FACE,{"disambiguationData":[OSD([sQuery(id+"F17.wireOp",EDGE,"E15")])]});
            var sketch = newSketch(context, id + "F29", { "sketchPlane" : qUnion([Q0])});
            skCircle(sketch, "E135", {"center": v(0, 0) * mm, "radius": 6.74 * mm});
            skCircle(sketch, "E136", {"center": v(0, 0) * mm, "radius": 11.63 * mm});
            skCircle(sketch, "E137", {"center": v(0, 0) * mm, "radius": 16.5 * mm});
            skCircle(sketch, "E138", {"center": v(0, 0) * mm, "radius": 23.5 * mm});
            skSolve(sketch);
        }
        {
            var Q0;
            Q0=makeQuery(id+"F20.opRevolve","SWEPT_FACE",FACE,{"disambiguationData":[OSD([sQuery(id+"F19.wireOp",EDGE,"E28")])]});
            var sketch = newSketch(context, id + "F30", { "sketchPlane" : qUnion([Q0])});
            skCircle(sketch, "E139", {"center": v(0, 0) * mm, "radius": 5.5 * mm});
            skCircle(sketch, "E140", {"center": v(0, 0) * mm, "radius": 11.5 * mm});
            skCircle(sketch, "E141", {"center": v(0, 0) * mm, "radius": 16 * mm});
            skCircle(sketch, "E142", {"center": v(0, 0) * mm, "radius": 8.5 * mm});
            skSolve(sketch);
        }
        {
            var Q0;
            Q0=makeQuery(id+"F20.opRevolve","SWEPT_FACE",FACE,{"disambiguationData":[OSD([sQuery(id+"F19.wireOp",EDGE,"E30")])]});
            var sketch = newSketch(context, id + "F31", { "sketchPlane" : qUnion([Q0])});
            skCircle(sketch, "E143", {"center": v(0, 0) * mm, "radius": 15.84 * mm});
            skCircle(sketch, "E144", {"center": v(0, 0) * mm, "radius": 17.86 * mm});
            skCircle(sketch, "E145", {"center": v(0, 0) * mm, "radius": 21.71 * mm});
            skSolve(sketch);
        }
        {
            var Q0;
            {var subQ0=sQuery(id+"F28.wireOp",EDGE,"E113.11.0");var subQ1=sQuery(id+"F17.wireOp",EDGE,"E15");var subQ2=makeQuery(id+"F18.opRevolve","SWEPT_EDGE",EDGE,{"disambiguationData":[OSD([subQ1,sQuery(id+"F17.wireOp",EDGE,"E27")])]});var subQ3=makeQuery(id+"F28.imprint","INTERSECT",VERTEX,{"derivedFrom":[subQ2,subQ0]});Q0=makeQuery(id+"F28.imprint","IMPRINT",FACE,{"disambiguationData":[TD([[makeQuery(id+"F28.imprint","IMPRINT",EDGE,{"disambiguationData":[TD([[subQ3,-1.0]])],"derivedFrom":subQ0}),1.0]])]});}
            var Q1;
            {var subQ0=sQuery(id+"F28.wireOp",EDGE,"E113.13.0");var subQ1=sQuery(id+"F17.wireOp",EDGE,"E15");var subQ2=makeQuery(id+"F18.opRevolve","SWEPT_EDGE",EDGE,{"disambiguationData":[OSD([subQ1,sQuery(id+"F17.wireOp",EDGE,"E27")])]});var subQ3=makeQuery(id+"F28.imprint","INTERSECT",VERTEX,{"derivedFrom":[subQ2,subQ0]});Q1=makeQuery(id+"F28.imprint","IMPRINT",FACE,{"disambiguationData":[TD([[makeQuery(id+"F28.imprint","IMPRINT",EDGE,{"disambiguationData":[TD([[subQ3,-1.0]])],"derivedFrom":subQ0}),1.0]])]});}
            var Q2;
            {var subQ0=sQuery(id+"F28.wireOp",EDGE,"E113.15.0");var subQ1=sQuery(id+"F17.wireOp",EDGE,"E15");var subQ2=makeQuery(id+"F18.opRevolve","SWEPT_EDGE",EDGE,{"disambiguationData":[OSD([subQ1,sQuery(id+"F17.wireOp",EDGE,"E27")])]});var subQ3=makeQuery(id+"F28.imprint","INTERSECT",VERTEX,{"derivedFrom":[subQ2,subQ0]});Q2=makeQuery(id+"F28.imprint","IMPRINT",FACE,{"disambiguationData":[TD([[makeQuery(id+"F28.imprint","IMPRINT",EDGE,{"disambiguationData":[TD([[subQ3,-1.0]])],"derivedFrom":subQ0}),1.0]])]});}
            var Q3;
            {var subQ0=sQuery(id+"F28.wireOp",EDGE,"E113.17.0");var subQ1=sQuery(id+"F17.wireOp",EDGE,"E15");var subQ2=makeQuery(id+"F18.opRevolve","SWEPT_EDGE",EDGE,{"disambiguationData":[OSD([subQ1,sQuery(id+"F17.wireOp",EDGE,"E27")])]});var subQ3=makeQuery(id+"F28.imprint","INTERSECT",VERTEX,{"derivedFrom":[subQ2,subQ0]});Q3=makeQuery(id+"F28.imprint","IMPRINT",FACE,{"disambiguationData":[TD([[makeQuery(id+"F28.imprint","IMPRINT",EDGE,{"disambiguationData":[TD([[subQ3,-1.0]])],"derivedFrom":subQ0}),1.0]])]});}
            var Q4;
            {var subQ0=sQuery(id+"F28.wireOp",EDGE,"E112");var subQ1=sQuery(id+"F17.wireOp",EDGE,"E15");var subQ2=makeQuery(id+"F18.opRevolve","SWEPT_EDGE",EDGE,{"disambiguationData":[OSD([subQ1,sQuery(id+"F17.wireOp",EDGE,"E27")])]});var subQ3=makeQuery(id+"F28.imprint","INTERSECT",VERTEX,{"derivedFrom":[subQ2,subQ0]});Q4=makeQuery(id+"F28.imprint","IMPRINT",FACE,{"disambiguationData":[TD([[makeQuery(id+"F28.imprint","IMPRINT",EDGE,{"disambiguationData":[TD([[subQ3,-1.0]])],"derivedFrom":subQ0}),-1.0]])]});}
            var Q5;
            {var subQ0=sQuery(id+"F28.wireOp",EDGE,"E113.1.0");var subQ1=sQuery(id+"F17.wireOp",EDGE,"E15");var subQ2=makeQuery(id+"F18.opRevolve","SWEPT_EDGE",EDGE,{"disambiguationData":[OSD([subQ1,sQuery(id+"F17.wireOp",EDGE,"E27")])]});var subQ3=makeQuery(id+"F28.imprint","INTERSECT",VERTEX,{"derivedFrom":[subQ2,subQ0]});Q5=makeQuery(id+"F28.imprint","IMPRINT",FACE,{"disambiguationData":[TD([[makeQuery(id+"F28.imprint","IMPRINT",EDGE,{"disambiguationData":[TD([[subQ3,-1.0]])],"derivedFrom":subQ0}),1.0]])]});}
            var Q6;
            {var subQ0=sQuery(id+"F28.wireOp",EDGE,"E113.3.0");var subQ1=sQuery(id+"F17.wireOp",EDGE,"E15");var subQ2=makeQuery(id+"F18.opRevolve","SWEPT_EDGE",EDGE,{"disambiguationData":[OSD([subQ1,sQuery(id+"F17.wireOp",EDGE,"E27")])]});var subQ3=makeQuery(id+"F28.imprint","INTERSECT",VERTEX,{"derivedFrom":[subQ2,subQ0]});Q6=makeQuery(id+"F28.imprint","IMPRINT",FACE,{"disambiguationData":[TD([[makeQuery(id+"F28.imprint","IMPRINT",EDGE,{"disambiguationData":[TD([[subQ3,-1.0]])],"derivedFrom":subQ0}),1.0]])]});}
            var Q7;
            {var subQ0=sQuery(id+"F28.wireOp",EDGE,"E113.5.0");var subQ1=sQuery(id+"F17.wireOp",EDGE,"E15");var subQ2=makeQuery(id+"F18.opRevolve","SWEPT_EDGE",EDGE,{"disambiguationData":[OSD([subQ1,sQuery(id+"F17.wireOp",EDGE,"E27")])]});var subQ3=makeQuery(id+"F28.imprint","INTERSECT",VERTEX,{"derivedFrom":[subQ2,subQ0]});Q7=makeQuery(id+"F28.imprint","IMPRINT",FACE,{"disambiguationData":[TD([[makeQuery(id+"F28.imprint","IMPRINT",EDGE,{"disambiguationData":[TD([[subQ3,-1.0]])],"derivedFrom":subQ0}),1.0]])]});}
            var Q8;
            {var subQ0=sQuery(id+"F28.wireOp",EDGE,"E113.7.0");var subQ1=sQuery(id+"F17.wireOp",EDGE,"E15");var subQ2=makeQuery(id+"F18.opRevolve","SWEPT_EDGE",EDGE,{"disambiguationData":[OSD([subQ1,sQuery(id+"F17.wireOp",EDGE,"E27")])]});var subQ3=makeQuery(id+"F28.imprint","INTERSECT",VERTEX,{"derivedFrom":[subQ2,subQ0]});Q8=makeQuery(id+"F28.imprint","IMPRINT",FACE,{"disambiguationData":[TD([[makeQuery(id+"F28.imprint","IMPRINT",EDGE,{"disambiguationData":[TD([[subQ3,-1.0]])],"derivedFrom":subQ0}),1.0]])]});}
            var Q9;
            {var subQ0=sQuery(id+"F28.wireOp",EDGE,"E113.9.0");var subQ1=sQuery(id+"F17.wireOp",EDGE,"E15");var subQ2=makeQuery(id+"F18.opRevolve","SWEPT_EDGE",EDGE,{"disambiguationData":[OSD([subQ1,sQuery(id+"F17.wireOp",EDGE,"E27")])]});var subQ3=makeQuery(id+"F28.imprint","INTERSECT",VERTEX,{"derivedFrom":[subQ2,subQ0]});Q9=makeQuery(id+"F28.imprint","IMPRINT",FACE,{"disambiguationData":[TD([[makeQuery(id+"F28.imprint","IMPRINT",EDGE,{"disambiguationData":[TD([[subQ3,-1.0]])],"derivedFrom":subQ0}),1.0]])]});}
            extrude(context, id + "F32", {"entities" : qUnion([Q0, Q1, Q2, Q3, Q4, Q5, Q6, Q7, Q8, Q9]), "operationType" : NewBodyOperationType.REMOVE, "oppositeDirection" : true, "depth" : 25 * mm, "offsetDistance" : 25 * mm, "hasDraft" : true, "draftAngle" : 45 * degree, "draftPullDirection" : true});
        }
        {
            var Q0;
            {var subQ0=sQuery(id+"F28.wireOp",EDGE,"E113.12.0");var subQ1=sQuery(id+"F17.wireOp",EDGE,"E15");var subQ2=makeQuery(id+"F18.opRevolve","SWEPT_EDGE",EDGE,{"disambiguationData":[OSD([subQ1,sQuery(id+"F17.wireOp",EDGE,"E27")])]});var subQ3=makeQuery(id+"F28.imprint","INTERSECT",VERTEX,{"derivedFrom":[subQ2,subQ0]});Q0=makeQuery(id+"F28.imprint","IMPRINT",FACE,{"disambiguationData":[TD([[makeQuery(id+"F28.imprint","IMPRINT",EDGE,{"disambiguationData":[TD([[subQ3,-1.0]])],"derivedFrom":subQ0}),1.0]])]});}
            var Q1;
            {var subQ0=sQuery(id+"F28.wireOp",EDGE,"E113.10.0");var subQ1=sQuery(id+"F17.wireOp",EDGE,"E15");var subQ2=makeQuery(id+"F18.opRevolve","SWEPT_EDGE",EDGE,{"disambiguationData":[OSD([subQ1,sQuery(id+"F17.wireOp",EDGE,"E27")])]});var subQ3=makeQuery(id+"F28.imprint","INTERSECT",VERTEX,{"derivedFrom":[subQ2,subQ0]});Q1=makeQuery(id+"F28.imprint","IMPRINT",FACE,{"disambiguationData":[TD([[makeQuery(id+"F28.imprint","IMPRINT",EDGE,{"disambiguationData":[TD([[subQ3,-1.0]])],"derivedFrom":subQ0}),1.0]])]});}
            var Q2;
            {var subQ0=sQuery(id+"F28.wireOp",EDGE,"E113.8.0");var subQ1=sQuery(id+"F17.wireOp",EDGE,"E15");var subQ2=makeQuery(id+"F18.opRevolve","SWEPT_EDGE",EDGE,{"disambiguationData":[OSD([subQ1,sQuery(id+"F17.wireOp",EDGE,"E27")])]});var subQ3=makeQuery(id+"F28.imprint","INTERSECT",VERTEX,{"derivedFrom":[subQ2,subQ0]});Q2=makeQuery(id+"F28.imprint","IMPRINT",FACE,{"disambiguationData":[TD([[makeQuery(id+"F28.imprint","IMPRINT",EDGE,{"disambiguationData":[TD([[subQ3,-1.0]])],"derivedFrom":subQ0}),1.0]])]});}
            var Q3;
            {var subQ0=sQuery(id+"F28.wireOp",EDGE,"E113.6.0");var subQ1=sQuery(id+"F17.wireOp",EDGE,"E15");var subQ2=makeQuery(id+"F18.opRevolve","SWEPT_EDGE",EDGE,{"disambiguationData":[OSD([subQ1,sQuery(id+"F17.wireOp",EDGE,"E27")])]});var subQ3=makeQuery(id+"F28.imprint","INTERSECT",VERTEX,{"derivedFrom":[subQ2,subQ0]});Q3=makeQuery(id+"F28.imprint","IMPRINT",FACE,{"disambiguationData":[TD([[makeQuery(id+"F28.imprint","IMPRINT",EDGE,{"disambiguationData":[TD([[subQ3,-1.0]])],"derivedFrom":subQ0}),1.0]])]});}
            var Q4;
            {var subQ0=sQuery(id+"F28.wireOp",EDGE,"E113.4.0");var subQ1=sQuery(id+"F17.wireOp",EDGE,"E15");var subQ2=makeQuery(id+"F18.opRevolve","SWEPT_EDGE",EDGE,{"disambiguationData":[OSD([subQ1,sQuery(id+"F17.wireOp",EDGE,"E27")])]});var subQ3=makeQuery(id+"F28.imprint","INTERSECT",VERTEX,{"derivedFrom":[subQ2,subQ0]});Q4=makeQuery(id+"F28.imprint","IMPRINT",FACE,{"disambiguationData":[TD([[makeQuery(id+"F28.imprint","IMPRINT",EDGE,{"disambiguationData":[TD([[subQ3,-1.0]])],"derivedFrom":subQ0}),1.0]])]});}
            var Q5;
            {var subQ0=sQuery(id+"F28.wireOp",EDGE,"E113.2.0");var subQ1=sQuery(id+"F17.wireOp",EDGE,"E15");var subQ2=makeQuery(id+"F18.opRevolve","SWEPT_EDGE",EDGE,{"disambiguationData":[OSD([subQ1,sQuery(id+"F17.wireOp",EDGE,"E27")])]});var subQ3=makeQuery(id+"F28.imprint","INTERSECT",VERTEX,{"derivedFrom":[subQ2,subQ0]});Q5=makeQuery(id+"F28.imprint","IMPRINT",FACE,{"disambiguationData":[TD([[makeQuery(id+"F28.imprint","IMPRINT",EDGE,{"disambiguationData":[TD([[subQ3,-1.0]])],"derivedFrom":subQ0}),1.0]])]});}
            var Q6;
            {var subQ0=sQuery(id+"F28.wireOp",EDGE,"E112");var subQ1=sQuery(id+"F17.wireOp",EDGE,"E15");var subQ2=makeQuery(id+"F18.opRevolve","SWEPT_EDGE",EDGE,{"disambiguationData":[OSD([subQ1,sQuery(id+"F17.wireOp",EDGE,"E27")])]});var subQ3=makeQuery(id+"F28.imprint","INTERSECT",VERTEX,{"derivedFrom":[subQ2,subQ0]});Q6=makeQuery(id+"F28.imprint","IMPRINT",FACE,{"disambiguationData":[TD([[makeQuery(id+"F28.imprint","IMPRINT",EDGE,{"disambiguationData":[TD([[subQ3,-1.0]])],"derivedFrom":subQ0}),1.0]])]});}
            var Q7;
            {var subQ0=sQuery(id+"F28.wireOp",EDGE,"E113.18.0");var subQ1=sQuery(id+"F17.wireOp",EDGE,"E15");var subQ2=makeQuery(id+"F18.opRevolve","SWEPT_EDGE",EDGE,{"disambiguationData":[OSD([subQ1,sQuery(id+"F17.wireOp",EDGE,"E27")])]});var subQ3=makeQuery(id+"F28.imprint","INTERSECT",VERTEX,{"derivedFrom":[subQ2,subQ0]});Q7=makeQuery(id+"F28.imprint","IMPRINT",FACE,{"disambiguationData":[TD([[makeQuery(id+"F28.imprint","IMPRINT",EDGE,{"disambiguationData":[TD([[subQ3,-1.0]])],"derivedFrom":subQ0}),1.0]])]});}
            var Q8;
            {var subQ0=sQuery(id+"F28.wireOp",EDGE,"E113.16.0");var subQ1=sQuery(id+"F17.wireOp",EDGE,"E15");var subQ2=makeQuery(id+"F18.opRevolve","SWEPT_EDGE",EDGE,{"disambiguationData":[OSD([subQ1,sQuery(id+"F17.wireOp",EDGE,"E27")])]});var subQ3=makeQuery(id+"F28.imprint","INTERSECT",VERTEX,{"derivedFrom":[subQ2,subQ0]});Q8=makeQuery(id+"F28.imprint","IMPRINT",FACE,{"disambiguationData":[TD([[makeQuery(id+"F28.imprint","IMPRINT",EDGE,{"disambiguationData":[TD([[subQ3,-1.0]])],"derivedFrom":subQ0}),1.0]])]});}
            var Q9;
            {var subQ0=sQuery(id+"F28.wireOp",EDGE,"E113.14.0");var subQ1=sQuery(id+"F17.wireOp",EDGE,"E15");var subQ2=makeQuery(id+"F18.opRevolve","SWEPT_EDGE",EDGE,{"disambiguationData":[OSD([subQ1,sQuery(id+"F17.wireOp",EDGE,"E27")])]});var subQ3=makeQuery(id+"F28.imprint","INTERSECT",VERTEX,{"derivedFrom":[subQ2,subQ0]});Q9=makeQuery(id+"F28.imprint","IMPRINT",FACE,{"disambiguationData":[TD([[makeQuery(id+"F28.imprint","IMPRINT",EDGE,{"disambiguationData":[TD([[subQ3,-1.0]])],"derivedFrom":subQ0}),1.0]])]});}
            extrude(context, id + "F33", {"entities" : qUnion([Q0, Q1, Q2, Q3, Q4, Q5, Q6, Q7, Q8, Q9]), "operationType" : NewBodyOperationType.REMOVE, "oppositeDirection" : true, "depth" : 25 * mm, "offsetDistance" : 25 * mm, "hasDraft" : true, "draftAngle" : 45 * degree, "draftPullDirection" : true});
        }
        {
            var Q0;
            Q0=makeQuery(id+"F18.opRevolve","SWEPT_FACE",FACE,{"disambiguationData":[OSD([sQuery(id+"F17.wireOp",EDGE,"E13")])]});
            var sketch = newSketch(context, id + "F34", { "sketchPlane" : qUnion([Q0])});
            skLineSegment(sketch, "E146", {"start": v(-0.01, 0.04) * mm, "end": v(32.49, 0.04) * mm});
            skLineSegment(sketch, "E147.1.0", {"start": v(-0.01, 0.04) * mm, "end": v(19.02, 6.23) * mm});
            skLineSegment(sketch, "E147.2.0", {"start": v(-0.01, 0.04) * mm, "end": v(16.18, 11.8) * mm});
            skLineSegment(sketch, "E147.3.0", {"start": v(-0.01, 0.04) * mm, "end": v(19.09, 26.33) * mm});
            skLineSegment(sketch, "E147.4.0", {"start": v(-0.01, 0.04) * mm, "end": v(10.03, 30.95) * mm});
            skLineSegment(sketch, "E147.5.0", {"start": v(-0.01, 0.04) * mm, "end": v(-0.01, 32.54) * mm});
            skLineSegment(sketch, "E147.6.0", {"start": v(-0.01, 0.04) * mm, "end": v(-10.06, 30.95) * mm});
            skLineSegment(sketch, "E147.7.0", {"start": v(-0.01, 0.04) * mm, "end": v(-19.12, 26.33) * mm});
            skLineSegment(sketch, "E147.8.0", {"start": v(-0.01, 0.04) * mm, "end": v(-26.3, 19.14) * mm});
            skLineSegment(sketch, "E147.9.0", {"start": v(-0.01, 0.04) * mm, "end": v(-19.05, 6.23) * mm});
            skLineSegment(sketch, "E147.10.0", {"start": v(-0.01, 0.04) * mm, "end": v(-32.51, 0.04) * mm});
            skLineSegment(sketch, "E147.11.0", {"start": v(-0.01, 0.04) * mm, "end": v(-30.92, -10) * mm});
            skLineSegment(sketch, "E147.12.0", {"start": v(-0.01, 0.04) * mm, "end": v(-16.2, -11.72) * mm});
            skLineSegment(sketch, "E147.13.0", {"start": v(-0.01, 0.04) * mm, "end": v(-19.12, -26.25) * mm});
            skLineSegment(sketch, "E147.14.0", {"start": v(-0.01, 0.04) * mm, "end": v(-6.2, -19) * mm});
            skLineSegment(sketch, "E147.15.0", {"start": v(-0.01, 0.04) * mm, "end": v(-0.01, -19.97) * mm});
            skLineSegment(sketch, "E147.16.0", {"start": v(-0.01, 0.04) * mm, "end": v(6.17, -19) * mm});
            skLineSegment(sketch, "E147.17.0", {"start": v(-0.01, 0.04) * mm, "end": v(19.09, -26.25) * mm});
            skLineSegment(sketch, "E147.18.0", {"start": v(-0.01, 0.04) * mm, "end": v(16.18, -11.72) * mm});
            skLineSegment(sketch, "E147.19.0", {"start": v(-0.01, 0.04) * mm, "end": v(30.9, -10) * mm});
            skPoint(sketch, "E147.center", {"position": v(-0.01, 0.04) * mm});
            skCircle(sketch, "E148", {"center": v(-0.01, 0.04) * mm, "radius": 32.5 * mm});
            skArc(sketch, "E149", {"start": v(-16.2, 11.8) * mm, "mid": v(-19.05, 6.23) * mm, "end": v(-20.03, 0.04) * mm});
            skArc(sketch, "E150", {"start": v(-11.78, 16.23) * mm, "mid": v(-14.17, 14.2) * mm, "end": v(-16.2, 11.8) * mm});
            skArc(sketch, "E151", {"start": v(-6.2, 19.08) * mm, "mid": v(-9.1, 17.87) * mm, "end": v(-11.78, 16.23) * mm});
            skArc(sketch, "E152", {"start": v(-0.01, 20.06) * mm, "mid": v(-3.14, 19.81) * mm, "end": v(-6.2, 19.08) * mm});
            skArc(sketch, "E153", {"start": v(6.17, 19.08) * mm, "mid": v(3.12, 19.81) * mm, "end": v(-0.01, 20.06) * mm});
            skArc(sketch, "E154", {"start": v(11.75, 16.23) * mm, "mid": v(9.07, 17.87) * mm, "end": v(6.17, 19.08) * mm});
            skLineSegment(sketch, "E155", {"start": v(16.18, 11.8) * mm, "end": v(26.28, 19.14) * mm});
            skLineSegment(sketch, "E156", {"start": v(19.02, 6.23) * mm, "end": v(30.9, 10.08) * mm});
            skArc(sketch, "E157", {"start": v(20, 0.04) * mm, "mid": v(17.82, 9.13) * mm, "end": v(11.75, 16.23) * mm});
            skArc(sketch, "E158", {"start": v(19.02, -6.14) * mm, "mid": v(19.75, -3.09) * mm, "end": v(20, 0.04) * mm});
            skLineSegment(sketch, "E159", {"start": v(16.18, -11.72) * mm, "end": v(26.28, -19.06) * mm});
            skArc(sketch, "E160", {"start": v(11.75, -16.15) * mm, "mid": v(16.18, -11.72) * mm, "end": v(19.02, -6.14) * mm});
            skLineSegment(sketch, "E161", {"start": v(6.17, -19) * mm, "end": v(10.03, -30.87) * mm});
            skLineSegment(sketch, "E162", {"start": v(-0.01, -19.97) * mm, "end": v(-0.01, -32.46) * mm});
            skLineSegment(sketch, "E163", {"start": v(-6.2, -19) * mm, "end": v(-10.06, -30.87) * mm});
            skArc(sketch, "E164", {"start": v(-11.78, -16.15) * mm, "mid": v(-0.01, -19.97) * mm, "end": v(11.75, -16.15) * mm});
            skLineSegment(sketch, "E165", {"start": v(-16.2, -11.72) * mm, "end": v(-26.3, -19.06) * mm});
            skArc(sketch, "E166", {"start": v(-19.05, -6.14) * mm, "mid": v(-16.2, -11.72) * mm, "end": v(-11.78, -16.15) * mm});
            skArc(sketch, "E167", {"start": v(-20.03, 0.04) * mm, "mid": v(-19.78, -3.09) * mm, "end": v(-19.05, -6.14) * mm});
            skLineSegment(sketch, "E168", {"start": v(-19.05, 6.23) * mm, "end": v(-30.92, 10.08) * mm});
            skSolve(sketch);
        }
        {
            var Q0;
            {var subQ5=sQuery(id+"F34.wireOp",EDGE,"E165");Q0=makeQuery(id+"F34.imprint","IMPRINT",FACE,{"disambiguationData":[TD([[makeQuery(id+"F34.imprint","IMPRINT",EDGE,{"derivedFrom":subQ5}),-1.0]])]});}
            var Q1;
            {var subQ0=sQuery(id+"F34.wireOp",EDGE,"E149");var subQ1=sQuery(id+"F34.wireOp",EDGE,"E147.10.0");var subQ2=makeQuery(id+"F34.imprint","INTERSECT",VERTEX,{"derivedFrom":[subQ1,subQ0,sQuery(id+"F34.wireOp",EDGE,"E167")]});Q1=makeQuery(id+"F34.imprint","IMPRINT",FACE,{"disambiguationData":[TD([[makeQuery(id+"F34.imprint","IMPRINT",EDGE,{"disambiguationData":[TD([[subQ2,-1.0]])],"derivedFrom":subQ1}),-1.0]])]});}
            var Q2;
            {var subQ0=sQuery(id+"F34.wireOp",EDGE,"E150");Q2=makeQuery(id+"F34.imprint","IMPRINT",FACE,{"disambiguationData":[TD([[makeQuery(id+"F34.imprint","IMPRINT",EDGE,{"derivedFrom":subQ0}),-1.0]])]});}
            var Q3;
            {var subQ0=sQuery(id+"F34.wireOp",EDGE,"E152");Q3=makeQuery(id+"F34.imprint","IMPRINT",FACE,{"disambiguationData":[TD([[makeQuery(id+"F34.imprint","IMPRINT",EDGE,{"derivedFrom":subQ0}),-1.0]])]});}
            var Q4;
            {var subQ0=sQuery(id+"F34.wireOp",EDGE,"E154");Q4=makeQuery(id+"F34.imprint","IMPRINT",FACE,{"disambiguationData":[TD([[makeQuery(id+"F34.imprint","IMPRINT",EDGE,{"derivedFrom":subQ0}),-1.0]])]});}
            var Q5;
            {var subQ0=sQuery(id+"F34.wireOp",EDGE,"E157");var subQ1=sQuery(id+"F34.wireOp",EDGE,"E155");var subQ2=makeQuery(id+"F34.imprint","INTERSECT",VERTEX,{"derivedFrom":[sQuery(id+"F34.wireOp",EDGE,"E147.2.0"),subQ1,subQ0]});Q5=makeQuery(id+"F34.imprint","IMPRINT",FACE,{"disambiguationData":[TD([[makeQuery(id+"F34.imprint","IMPRINT",EDGE,{"disambiguationData":[TD([[subQ2,-1.0]])],"derivedFrom":subQ1}),-1.0]])]});}
            var Q6;
            {var subQ3=sQuery(id+"F34.wireOp",EDGE,"E158");Q6=makeQuery(id+"F34.imprint","IMPRINT",FACE,{"disambiguationData":[TD([[makeQuery(id+"F34.imprint","IMPRINT",EDGE,{"derivedFrom":subQ3}),-1.0]])]});}
            var Q7;
            {var subQ5=sQuery(id+"F34.wireOp",EDGE,"E159");Q7=makeQuery(id+"F34.imprint","IMPRINT",FACE,{"disambiguationData":[TD([[makeQuery(id+"F34.imprint","IMPRINT",EDGE,{"derivedFrom":subQ5}),-1.0]])]});}
            var Q8;
            {var subQ0=sQuery(id+"F34.wireOp",EDGE,"E161");Q8=makeQuery(id+"F34.imprint","IMPRINT",FACE,{"disambiguationData":[TD([[makeQuery(id+"F34.imprint","IMPRINT",EDGE,{"derivedFrom":subQ0}),-1.0]])]});}
            var Q9;
            {var subQ5=sQuery(id+"F34.wireOp",EDGE,"E163");Q9=makeQuery(id+"F34.imprint","IMPRINT",FACE,{"disambiguationData":[TD([[makeQuery(id+"F34.imprint","IMPRINT",EDGE,{"derivedFrom":subQ5}),-1.0]])]});}
            var Q10;
            {var subQ0=sQuery(id+"F34.wireOp",EDGE,"E158");var subQ1=sQuery(id+"F34.wireOp",EDGE,"E146");var subQ2=makeQuery(id+"F34.imprint","INTERSECT",VERTEX,{"derivedFrom":[subQ1,sQuery(id+"F34.wireOp",EDGE,"E157"),subQ0]});Q10=makeQuery(id+"F34.imprint","IMPRINT",FACE,{"disambiguationData":[TD([[makeQuery(id+"F34.imprint","IMPRINT",EDGE,{"disambiguationData":[TD([[subQ2,-1.0]])],"derivedFrom":subQ1}),-1.0]])]});}
            extrude(context, id + "F35", {"entities" : qUnion([Q0, Q1, Q2, Q3, Q4, Q5, Q6, Q7, Q8, Q9, Q10]), "operationType" : NewBodyOperationType.REMOVE, "oppositeDirection" : true, "depth" : 25 * mm, "offsetDistance" : 25 * mm, "hasDraft" : true, "draftAngle" : 45 * degree, "draftPullDirection" : true});
        }
        {
            var Q0;
            {var subQ0=sQuery(id+"F34.wireOp",EDGE,"E157");var subQ1=sQuery(id+"F34.wireOp",EDGE,"E146");var subQ2=makeQuery(id+"F34.imprint","INTERSECT",VERTEX,{"derivedFrom":[subQ1,subQ0,sQuery(id+"F34.wireOp",EDGE,"E158")]});Q0=makeQuery(id+"F34.imprint","IMPRINT",FACE,{"disambiguationData":[TD([[makeQuery(id+"F34.imprint","IMPRINT",EDGE,{"disambiguationData":[TD([[subQ2,-1.0]])],"derivedFrom":subQ1}),1.0]])]});}
            var Q1;
            {var subQ0=sQuery(id+"F34.wireOp",EDGE,"E157");var subQ1=sQuery(id+"F34.wireOp",EDGE,"E147.3.0");var subQ2=makeQuery(id+"F34.imprint","INTERSECT",VERTEX,{"derivedFrom":[subQ1,sQuery(id+"F34.wireOp",EDGE,"E154"),subQ0]});Q1=makeQuery(id+"F34.imprint","IMPRINT",FACE,{"disambiguationData":[TD([[makeQuery(id+"F34.imprint","IMPRINT",EDGE,{"disambiguationData":[TD([[subQ2,-1.0]])],"derivedFrom":subQ1}),-1.0]])]});}
            var Q2;
            {var subQ0=sQuery(id+"F34.wireOp",EDGE,"E153");Q2=makeQuery(id+"F34.imprint","IMPRINT",FACE,{"disambiguationData":[TD([[makeQuery(id+"F34.imprint","IMPRINT",EDGE,{"derivedFrom":subQ0}),-1.0]])]});}
            var Q3;
            {var subQ0=sQuery(id+"F34.wireOp",EDGE,"E147.19.0");var subQ1=sQuery(id+"F17.wireOp",EDGE,"E13");var subQ2=makeQuery(id+"F18.opRevolve","SWEPT_EDGE",EDGE,{"disambiguationData":[OSD([subQ1,sQuery(id+"F17.wireOp",EDGE,"E14")])]});var subQ3=makeQuery(id+"F34.imprint","INTERSECT",VERTEX,{"derivedFrom":[subQ2,subQ0]});Q3=makeQuery(id+"F34.imprint","IMPRINT",FACE,{"disambiguationData":[TD([[makeQuery(id+"F34.imprint","IMPRINT",EDGE,{"disambiguationData":[TD([[subQ3,-1.0]])],"derivedFrom":subQ0}),-1.0]])]});}
            var Q4;
            {var subQ0=sQuery(id+"F34.wireOp",EDGE,"E147.17.0");var subQ1=sQuery(id+"F17.wireOp",EDGE,"E13");var subQ2=makeQuery(id+"F18.opRevolve","SWEPT_EDGE",EDGE,{"disambiguationData":[OSD([subQ1,sQuery(id+"F17.wireOp",EDGE,"E14")])]});var subQ3=makeQuery(id+"F34.imprint","INTERSECT",VERTEX,{"derivedFrom":[subQ2,subQ0]});Q4=makeQuery(id+"F34.imprint","IMPRINT",FACE,{"disambiguationData":[TD([[makeQuery(id+"F34.imprint","IMPRINT",EDGE,{"disambiguationData":[TD([[subQ3,-1.0]])],"derivedFrom":subQ0}),-1.0]])]});}
            var Q5;
            {var subQ0=sQuery(id+"F34.wireOp",EDGE,"E162");var subQ1=sQuery(id+"F17.wireOp",EDGE,"E13");var subQ2=makeQuery(id+"F18.opRevolve","SWEPT_EDGE",EDGE,{"disambiguationData":[OSD([subQ1,sQuery(id+"F17.wireOp",EDGE,"E14")])]});var subQ3=makeQuery(id+"F34.imprint","INTERSECT",VERTEX,{"derivedFrom":[subQ2,subQ0]});Q5=makeQuery(id+"F34.imprint","IMPRINT",FACE,{"disambiguationData":[TD([[makeQuery(id+"F34.imprint","IMPRINT",EDGE,{"disambiguationData":[TD([[subQ3,-1.0]])],"derivedFrom":subQ0}),-1.0]])]});}
            var Q6;
            {var subQ0=sQuery(id+"F34.wireOp",EDGE,"E147.13.0");var subQ1=sQuery(id+"F17.wireOp",EDGE,"E13");var subQ6=makeQuery(id+"F18.opRevolve","SWEPT_EDGE",EDGE,{"disambiguationData":[OSD([subQ1,sQuery(id+"F17.wireOp",EDGE,"E14")])]});var subQ7=makeQuery(id+"F34.imprint","INTERSECT",VERTEX,{"derivedFrom":[subQ6,subQ0]});Q6=makeQuery(id+"F34.imprint","IMPRINT",FACE,{"disambiguationData":[TD([[makeQuery(id+"F34.imprint","IMPRINT",EDGE,{"disambiguationData":[TD([[subQ7,-1.0]])],"derivedFrom":subQ0}),-1.0]])]});}
            var Q7;
            {var subQ0=sQuery(id+"F34.wireOp",EDGE,"E167");Q7=makeQuery(id+"F34.imprint","IMPRINT",FACE,{"disambiguationData":[TD([[makeQuery(id+"F34.imprint","IMPRINT",EDGE,{"derivedFrom":subQ0}),-1.0]])]});}
            var Q8;
            {var subQ0=sQuery(id+"F34.wireOp",EDGE,"E149");var subQ1=sQuery(id+"F34.wireOp",EDGE,"E147.8.0");var subQ2=makeQuery(id+"F34.imprint","INTERSECT",VERTEX,{"derivedFrom":[subQ1,subQ0,sQuery(id+"F34.wireOp",EDGE,"E150")]});Q8=makeQuery(id+"F34.imprint","IMPRINT",FACE,{"disambiguationData":[TD([[makeQuery(id+"F34.imprint","IMPRINT",EDGE,{"disambiguationData":[TD([[subQ2,-1.0]])],"derivedFrom":subQ1}),1.0]])]});}
            var Q9;
            {var subQ0=sQuery(id+"F34.wireOp",EDGE,"E151");Q9=makeQuery(id+"F34.imprint","IMPRINT",FACE,{"disambiguationData":[TD([[makeQuery(id+"F34.imprint","IMPRINT",EDGE,{"derivedFrom":subQ0}),-1.0]])]});}
            extrude(context, id + "F36", {"entities" : qUnion([Q0, Q1, Q2, Q3, Q4, Q5, Q6, Q7, Q8, Q9]), "operationType" : NewBodyOperationType.REMOVE, "oppositeDirection" : true, "depth" : 5 * mm, "offsetDistance" : 25 * mm, "hasDraft" : true, "draftAngle" : 45 * degree, "draftPullDirection" : true});
        }
        {
            var Q0;
            Q0=makeQuery(id+"F20.opRevolve","SWEPT_FACE",FACE,{"disambiguationData":[OSD([sQuery(id+"F19.wireOp",EDGE,"E28")])]});
            var sketch = newSketch(context, id + "F37", { "sketchPlane" : qUnion([Q0])});
            skLineSegment(sketch, "E169", {"start": v(-0.01, 0.04) * mm, "end": v(32.49, 0.04) * mm});
            skLineSegment(sketch, "E170.1.0", {"start": v(-0.01, 0.04) * mm, "end": v(19.02, 6.23) * mm});
            skLineSegment(sketch, "E170.2.0", {"start": v(-0.01, 0.04) * mm, "end": v(16.18, 11.8) * mm});
            skLineSegment(sketch, "E170.3.0", {"start": v(-0.01, 0.04) * mm, "end": v(19.09, 26.33) * mm});
            skLineSegment(sketch, "E170.4.0", {"start": v(-0.01, 0.04) * mm, "end": v(10.03, 30.95) * mm});
            skLineSegment(sketch, "E170.5.0", {"start": v(-0.01, 0.04) * mm, "end": v(-0.01, 32.54) * mm});
            skLineSegment(sketch, "E170.6.0", {"start": v(-0.01, 0.04) * mm, "end": v(-10.06, 30.95) * mm});
            skLineSegment(sketch, "E170.7.0", {"start": v(-0.01, 0.04) * mm, "end": v(-19.12, 26.33) * mm});
            skLineSegment(sketch, "E170.8.0", {"start": v(-0.01, 0.04) * mm, "end": v(-26.3, 19.14) * mm});
            skLineSegment(sketch, "E170.9.0", {"start": v(-0.01, 0.04) * mm, "end": v(-19.05, 6.23) * mm});
            skLineSegment(sketch, "E170.10.0", {"start": v(-0.01, 0.04) * mm, "end": v(-32.51, 0.04) * mm});
            skLineSegment(sketch, "E170.11.0", {"start": v(-0.01, 0.04) * mm, "end": v(-30.92, -10) * mm});
            skLineSegment(sketch, "E170.12.0", {"start": v(-0.01, 0.04) * mm, "end": v(-16.2, -11.72) * mm});
            skLineSegment(sketch, "E170.13.0", {"start": v(-0.01, 0.04) * mm, "end": v(-19.12, -26.25) * mm});
            skLineSegment(sketch, "E170.14.0", {"start": v(-0.01, 0.04) * mm, "end": v(-6.2, -19) * mm});
            skLineSegment(sketch, "E170.15.0", {"start": v(-0.01, 0.04) * mm, "end": v(-0.01, -19.97) * mm});
            skLineSegment(sketch, "E170.16.0", {"start": v(-0.01, 0.04) * mm, "end": v(6.17, -19) * mm});
            skLineSegment(sketch, "E170.17.0", {"start": v(-0.01, 0.04) * mm, "end": v(19.09, -26.25) * mm});
            skLineSegment(sketch, "E170.18.0", {"start": v(-0.01, 0.04) * mm, "end": v(16.18, -11.72) * mm});
            skLineSegment(sketch, "E170.19.0", {"start": v(-0.01, 0.04) * mm, "end": v(30.9, -10) * mm});
            skPoint(sketch, "E170.center", {"position": v(-0.01, 0.04) * mm});
            skCircle(sketch, "E171", {"center": v(-0.01, 0.04) * mm, "radius": 32.5 * mm});
            skArc(sketch, "E172", {"start": v(-16.2, 11.8) * mm, "mid": v(-19.05, 6.23) * mm, "end": v(-20.03, 0.04) * mm});
            skArc(sketch, "E173", {"start": v(-11.78, 16.23) * mm, "mid": v(-14.17, 14.2) * mm, "end": v(-16.2, 11.8) * mm});
            skArc(sketch, "E174", {"start": v(-6.2, 19.08) * mm, "mid": v(-9.1, 17.87) * mm, "end": v(-11.78, 16.23) * mm});
            skArc(sketch, "E175", {"start": v(-0.01, 20.06) * mm, "mid": v(-3.14, 19.81) * mm, "end": v(-6.2, 19.08) * mm});
            skArc(sketch, "E176", {"start": v(6.17, 19.08) * mm, "mid": v(3.12, 19.81) * mm, "end": v(-0.01, 20.06) * mm});
            skArc(sketch, "E177", {"start": v(11.75, 16.23) * mm, "mid": v(9.07, 17.87) * mm, "end": v(6.17, 19.08) * mm});
            skLineSegment(sketch, "E178", {"start": v(16.18, 11.8) * mm, "end": v(26.28, 19.14) * mm});
            skLineSegment(sketch, "E179", {"start": v(19.02, 6.23) * mm, "end": v(30.9, 10.08) * mm});
            skArc(sketch, "E180", {"start": v(20, 0.04) * mm, "mid": v(17.82, 9.13) * mm, "end": v(11.75, 16.23) * mm});
            skArc(sketch, "E181", {"start": v(19.02, -6.14) * mm, "mid": v(19.75, -3.09) * mm, "end": v(20, 0.04) * mm});
            skLineSegment(sketch, "E182", {"start": v(16.18, -11.72) * mm, "end": v(26.28, -19.06) * mm});
            skArc(sketch, "E183", {"start": v(11.75, -16.15) * mm, "mid": v(16.18, -11.72) * mm, "end": v(19.02, -6.14) * mm});
            skLineSegment(sketch, "E184", {"start": v(6.17, -19) * mm, "end": v(10.03, -30.87) * mm});
            skLineSegment(sketch, "E185", {"start": v(-0.01, -19.97) * mm, "end": v(-0.01, -32.46) * mm});
            skLineSegment(sketch, "E186", {"start": v(-6.2, -19) * mm, "end": v(-10.06, -30.87) * mm});
            skArc(sketch, "E187", {"start": v(-11.78, -16.15) * mm, "mid": v(-0.01, -19.97) * mm, "end": v(11.75, -16.15) * mm});
            skLineSegment(sketch, "E188", {"start": v(-16.2, -11.72) * mm, "end": v(-26.3, -19.06) * mm});
            skArc(sketch, "E189", {"start": v(-19.05, -6.14) * mm, "mid": v(-16.2, -11.72) * mm, "end": v(-11.78, -16.15) * mm});
            skArc(sketch, "E190", {"start": v(-20.03, 0.04) * mm, "mid": v(-19.78, -3.09) * mm, "end": v(-19.05, -6.14) * mm});
            skLineSegment(sketch, "E191", {"start": v(-19.05, 6.23) * mm, "end": v(-30.92, 10.08) * mm});
            skSolve(sketch);
        }
        {
            var Q0;
            {var subQ0=sQuery(id+"F37.wireOp",EDGE,"E169");var subQ1=sQuery(id+"F19.wireOp",EDGE,"E28");var subQ2=makeQuery(id+"F20.opRevolve","SWEPT_EDGE",EDGE,{"disambiguationData":[OSD([subQ1,sQuery(id+"F19.wireOp",EDGE,"E35")])]});var subQ3=makeQuery(id+"F37.imprint","INTERSECT",VERTEX,{"derivedFrom":[subQ2,subQ0]});Q0=makeQuery(id+"F37.imprint","IMPRINT",FACE,{"disambiguationData":[TD([[makeQuery(id+"F37.imprint","IMPRINT",EDGE,{"disambiguationData":[TD([[subQ3,-1.0]])],"derivedFrom":subQ0}),1.0]])]});}
            var Q1;
            {var subQ0=sQuery(id+"F37.wireOp",EDGE,"E170.2.0");var subQ1=sQuery(id+"F19.wireOp",EDGE,"E28");var subQ2=makeQuery(id+"F20.opRevolve","SWEPT_EDGE",EDGE,{"disambiguationData":[OSD([subQ1,sQuery(id+"F19.wireOp",EDGE,"E35")])]});var subQ3=makeQuery(id+"F37.imprint","INTERSECT",VERTEX,{"derivedFrom":[subQ2,subQ0]});Q1=makeQuery(id+"F37.imprint","IMPRINT",FACE,{"disambiguationData":[TD([[makeQuery(id+"F37.imprint","IMPRINT",EDGE,{"disambiguationData":[TD([[subQ3,-1.0]])],"derivedFrom":subQ0}),1.0]])]});}
            var Q2;
            {var subQ0=sQuery(id+"F37.wireOp",EDGE,"E170.4.0");var subQ1=sQuery(id+"F19.wireOp",EDGE,"E28");var subQ2=makeQuery(id+"F20.opRevolve","SWEPT_EDGE",EDGE,{"disambiguationData":[OSD([subQ1,sQuery(id+"F19.wireOp",EDGE,"E35")])]});var subQ3=makeQuery(id+"F37.imprint","INTERSECT",VERTEX,{"derivedFrom":[subQ2,subQ0]});Q2=makeQuery(id+"F37.imprint","IMPRINT",FACE,{"disambiguationData":[TD([[makeQuery(id+"F37.imprint","IMPRINT",EDGE,{"disambiguationData":[TD([[subQ3,-1.0]])],"derivedFrom":subQ0}),1.0]])]});}
            var Q3;
            {var subQ0=sQuery(id+"F37.wireOp",EDGE,"E170.6.0");var subQ1=sQuery(id+"F19.wireOp",EDGE,"E28");var subQ2=makeQuery(id+"F20.opRevolve","SWEPT_EDGE",EDGE,{"disambiguationData":[OSD([subQ1,sQuery(id+"F19.wireOp",EDGE,"E35")])]});var subQ3=makeQuery(id+"F37.imprint","INTERSECT",VERTEX,{"derivedFrom":[subQ2,subQ0]});Q3=makeQuery(id+"F37.imprint","IMPRINT",FACE,{"disambiguationData":[TD([[makeQuery(id+"F37.imprint","IMPRINT",EDGE,{"disambiguationData":[TD([[subQ3,-1.0]])],"derivedFrom":subQ0}),1.0]])]});}
            var Q4;
            {var subQ0=sQuery(id+"F37.wireOp",EDGE,"E170.8.0");var subQ1=sQuery(id+"F19.wireOp",EDGE,"E28");var subQ2=makeQuery(id+"F20.opRevolve","SWEPT_EDGE",EDGE,{"disambiguationData":[OSD([subQ1,sQuery(id+"F19.wireOp",EDGE,"E35")])]});var subQ3=makeQuery(id+"F37.imprint","INTERSECT",VERTEX,{"derivedFrom":[subQ2,subQ0]});Q4=makeQuery(id+"F37.imprint","IMPRINT",FACE,{"disambiguationData":[TD([[makeQuery(id+"F37.imprint","IMPRINT",EDGE,{"disambiguationData":[TD([[subQ3,-1.0]])],"derivedFrom":subQ0}),1.0]])]});}
            var Q5;
            {var subQ0=sQuery(id+"F37.wireOp",EDGE,"E170.10.0");var subQ1=sQuery(id+"F19.wireOp",EDGE,"E28");var subQ2=makeQuery(id+"F20.opRevolve","SWEPT_EDGE",EDGE,{"disambiguationData":[OSD([subQ1,sQuery(id+"F19.wireOp",EDGE,"E35")])]});var subQ3=makeQuery(id+"F37.imprint","INTERSECT",VERTEX,{"derivedFrom":[subQ2,subQ0]});Q5=makeQuery(id+"F37.imprint","IMPRINT",FACE,{"disambiguationData":[TD([[makeQuery(id+"F37.imprint","IMPRINT",EDGE,{"disambiguationData":[TD([[subQ3,-1.0]])],"derivedFrom":subQ0}),1.0]])]});}
            var Q6;
            {var subQ0=sQuery(id+"F37.wireOp",EDGE,"E170.12.0");var subQ1=sQuery(id+"F19.wireOp",EDGE,"E28");var subQ2=makeQuery(id+"F20.opRevolve","SWEPT_EDGE",EDGE,{"disambiguationData":[OSD([subQ1,sQuery(id+"F19.wireOp",EDGE,"E35")])]});var subQ3=makeQuery(id+"F37.imprint","INTERSECT",VERTEX,{"derivedFrom":[subQ2,subQ0]});Q6=makeQuery(id+"F37.imprint","IMPRINT",FACE,{"disambiguationData":[TD([[makeQuery(id+"F37.imprint","IMPRINT",EDGE,{"disambiguationData":[TD([[subQ3,-1.0]])],"derivedFrom":subQ0}),1.0]])]});}
            var Q7;
            {var subQ0=sQuery(id+"F37.wireOp",EDGE,"E170.14.0");var subQ1=sQuery(id+"F19.wireOp",EDGE,"E28");var subQ2=makeQuery(id+"F20.opRevolve","SWEPT_EDGE",EDGE,{"disambiguationData":[OSD([subQ1,sQuery(id+"F19.wireOp",EDGE,"E35")])]});var subQ3=makeQuery(id+"F37.imprint","INTERSECT",VERTEX,{"derivedFrom":[subQ2,subQ0]});Q7=makeQuery(id+"F37.imprint","IMPRINT",FACE,{"disambiguationData":[TD([[makeQuery(id+"F37.imprint","IMPRINT",EDGE,{"disambiguationData":[TD([[subQ3,-1.0]])],"derivedFrom":subQ0}),1.0]])]});}
            var Q8;
            {var subQ0=sQuery(id+"F37.wireOp",EDGE,"E170.16.0");var subQ1=sQuery(id+"F19.wireOp",EDGE,"E28");var subQ2=makeQuery(id+"F20.opRevolve","SWEPT_EDGE",EDGE,{"disambiguationData":[OSD([subQ1,sQuery(id+"F19.wireOp",EDGE,"E35")])]});var subQ3=makeQuery(id+"F37.imprint","INTERSECT",VERTEX,{"derivedFrom":[subQ2,subQ0]});Q8=makeQuery(id+"F37.imprint","IMPRINT",FACE,{"disambiguationData":[TD([[makeQuery(id+"F37.imprint","IMPRINT",EDGE,{"disambiguationData":[TD([[subQ3,-1.0]])],"derivedFrom":subQ0}),1.0]])]});}
            var Q9;
            {var subQ0=sQuery(id+"F37.wireOp",EDGE,"E170.18.0");var subQ1=sQuery(id+"F19.wireOp",EDGE,"E28");var subQ2=makeQuery(id+"F20.opRevolve","SWEPT_EDGE",EDGE,{"disambiguationData":[OSD([subQ1,sQuery(id+"F19.wireOp",EDGE,"E35")])]});var subQ3=makeQuery(id+"F37.imprint","INTERSECT",VERTEX,{"derivedFrom":[subQ2,subQ0]});Q9=makeQuery(id+"F37.imprint","IMPRINT",FACE,{"disambiguationData":[TD([[makeQuery(id+"F37.imprint","IMPRINT",EDGE,{"disambiguationData":[TD([[subQ3,-1.0]])],"derivedFrom":subQ0}),1.0]])]});}
            extrude(context, id + "F38", {"entities" : qUnion([Q0, Q1, Q2, Q3, Q4, Q5, Q6, Q7, Q8, Q9]), "operationType" : NewBodyOperationType.REMOVE, "oppositeDirection" : true, "depth" : 5 * mm, "offsetDistance" : 25 * mm, "hasDraft" : true, "draftAngle" : 45 * degree, "draftPullDirection" : true});
        }
        {
            var Q0;
            {var subQ0=sQuery(id+"F37.wireOp",EDGE,"E170.11.0");var subQ1=sQuery(id+"F19.wireOp",EDGE,"E28");var subQ2=makeQuery(id+"F20.opRevolve","SWEPT_EDGE",EDGE,{"disambiguationData":[OSD([subQ1,sQuery(id+"F19.wireOp",EDGE,"E35")])]});var subQ3=makeQuery(id+"F37.imprint","INTERSECT",VERTEX,{"derivedFrom":[subQ2,subQ0]});Q0=makeQuery(id+"F37.imprint","IMPRINT",FACE,{"disambiguationData":[TD([[makeQuery(id+"F37.imprint","IMPRINT",EDGE,{"disambiguationData":[TD([[subQ3,-1.0]])],"derivedFrom":subQ0}),1.0]])]});}
            var Q1;
            {var subQ0=sQuery(id+"F37.wireOp",EDGE,"E170.9.0");var subQ1=sQuery(id+"F19.wireOp",EDGE,"E28");var subQ2=makeQuery(id+"F20.opRevolve","SWEPT_EDGE",EDGE,{"disambiguationData":[OSD([subQ1,sQuery(id+"F19.wireOp",EDGE,"E35")])]});var subQ3=makeQuery(id+"F37.imprint","INTERSECT",VERTEX,{"derivedFrom":[subQ2,subQ0]});Q1=makeQuery(id+"F37.imprint","IMPRINT",FACE,{"disambiguationData":[TD([[makeQuery(id+"F37.imprint","IMPRINT",EDGE,{"disambiguationData":[TD([[subQ3,-1.0]])],"derivedFrom":subQ0}),1.0]])]});}
            var Q2;
            {var subQ0=sQuery(id+"F37.wireOp",EDGE,"E170.7.0");var subQ1=sQuery(id+"F19.wireOp",EDGE,"E28");var subQ2=makeQuery(id+"F20.opRevolve","SWEPT_EDGE",EDGE,{"disambiguationData":[OSD([subQ1,sQuery(id+"F19.wireOp",EDGE,"E35")])]});var subQ3=makeQuery(id+"F37.imprint","INTERSECT",VERTEX,{"derivedFrom":[subQ2,subQ0]});Q2=makeQuery(id+"F37.imprint","IMPRINT",FACE,{"disambiguationData":[TD([[makeQuery(id+"F37.imprint","IMPRINT",EDGE,{"disambiguationData":[TD([[subQ3,-1.0]])],"derivedFrom":subQ0}),1.0]])]});}
            var Q3;
            {var subQ0=sQuery(id+"F37.wireOp",EDGE,"E170.5.0");var subQ1=sQuery(id+"F19.wireOp",EDGE,"E28");var subQ2=makeQuery(id+"F20.opRevolve","SWEPT_EDGE",EDGE,{"disambiguationData":[OSD([subQ1,sQuery(id+"F19.wireOp",EDGE,"E35")])]});var subQ3=makeQuery(id+"F37.imprint","INTERSECT",VERTEX,{"derivedFrom":[subQ2,subQ0]});Q3=makeQuery(id+"F37.imprint","IMPRINT",FACE,{"disambiguationData":[TD([[makeQuery(id+"F37.imprint","IMPRINT",EDGE,{"disambiguationData":[TD([[subQ3,-1.0]])],"derivedFrom":subQ0}),1.0]])]});}
            var Q4;
            {var subQ0=sQuery(id+"F37.wireOp",EDGE,"E170.3.0");var subQ1=sQuery(id+"F19.wireOp",EDGE,"E28");var subQ2=makeQuery(id+"F20.opRevolve","SWEPT_EDGE",EDGE,{"disambiguationData":[OSD([subQ1,sQuery(id+"F19.wireOp",EDGE,"E35")])]});var subQ3=makeQuery(id+"F37.imprint","INTERSECT",VERTEX,{"derivedFrom":[subQ2,subQ0]});Q4=makeQuery(id+"F37.imprint","IMPRINT",FACE,{"disambiguationData":[TD([[makeQuery(id+"F37.imprint","IMPRINT",EDGE,{"disambiguationData":[TD([[subQ3,-1.0]])],"derivedFrom":subQ0}),1.0]])]});}
            var Q5;
            {var subQ0=sQuery(id+"F37.wireOp",EDGE,"E170.1.0");var subQ1=sQuery(id+"F19.wireOp",EDGE,"E28");var subQ2=makeQuery(id+"F20.opRevolve","SWEPT_EDGE",EDGE,{"disambiguationData":[OSD([subQ1,sQuery(id+"F19.wireOp",EDGE,"E35")])]});var subQ3=makeQuery(id+"F37.imprint","INTERSECT",VERTEX,{"derivedFrom":[subQ2,subQ0]});Q5=makeQuery(id+"F37.imprint","IMPRINT",FACE,{"disambiguationData":[TD([[makeQuery(id+"F37.imprint","IMPRINT",EDGE,{"disambiguationData":[TD([[subQ3,-1.0]])],"derivedFrom":subQ0}),1.0]])]});}
            var Q6;
            {var subQ0=sQuery(id+"F37.wireOp",EDGE,"E169");var subQ1=sQuery(id+"F19.wireOp",EDGE,"E28");var subQ2=makeQuery(id+"F20.opRevolve","SWEPT_EDGE",EDGE,{"disambiguationData":[OSD([subQ1,sQuery(id+"F19.wireOp",EDGE,"E35")])]});var subQ3=makeQuery(id+"F37.imprint","INTERSECT",VERTEX,{"derivedFrom":[subQ2,subQ0]});Q6=makeQuery(id+"F37.imprint","IMPRINT",FACE,{"disambiguationData":[TD([[makeQuery(id+"F37.imprint","IMPRINT",EDGE,{"disambiguationData":[TD([[subQ3,-1.0]])],"derivedFrom":subQ0}),-1.0]])]});}
            var Q7;
            {var subQ0=sQuery(id+"F37.wireOp",EDGE,"E170.17.0");var subQ1=sQuery(id+"F19.wireOp",EDGE,"E28");var subQ2=makeQuery(id+"F20.opRevolve","SWEPT_EDGE",EDGE,{"disambiguationData":[OSD([subQ1,sQuery(id+"F19.wireOp",EDGE,"E35")])]});var subQ3=makeQuery(id+"F37.imprint","INTERSECT",VERTEX,{"derivedFrom":[subQ2,subQ0]});Q7=makeQuery(id+"F37.imprint","IMPRINT",FACE,{"disambiguationData":[TD([[makeQuery(id+"F37.imprint","IMPRINT",EDGE,{"disambiguationData":[TD([[subQ3,-1.0]])],"derivedFrom":subQ0}),1.0]])]});}
            var Q8;
            {var subQ0=sQuery(id+"F37.wireOp",EDGE,"E170.15.0");var subQ1=sQuery(id+"F19.wireOp",EDGE,"E28");var subQ2=makeQuery(id+"F20.opRevolve","SWEPT_EDGE",EDGE,{"disambiguationData":[OSD([subQ1,sQuery(id+"F19.wireOp",EDGE,"E35")])]});var subQ3=makeQuery(id+"F37.imprint","INTERSECT",VERTEX,{"derivedFrom":[subQ2,subQ0]});Q8=makeQuery(id+"F37.imprint","IMPRINT",FACE,{"disambiguationData":[TD([[makeQuery(id+"F37.imprint","IMPRINT",EDGE,{"disambiguationData":[TD([[subQ3,-1.0]])],"derivedFrom":subQ0}),1.0]])]});}
            var Q9;
            {var subQ0=sQuery(id+"F37.wireOp",EDGE,"E170.13.0");var subQ1=sQuery(id+"F19.wireOp",EDGE,"E28");var subQ2=makeQuery(id+"F20.opRevolve","SWEPT_EDGE",EDGE,{"disambiguationData":[OSD([subQ1,sQuery(id+"F19.wireOp",EDGE,"E35")])]});var subQ3=makeQuery(id+"F37.imprint","INTERSECT",VERTEX,{"derivedFrom":[subQ2,subQ0]});Q9=makeQuery(id+"F37.imprint","IMPRINT",FACE,{"disambiguationData":[TD([[makeQuery(id+"F37.imprint","IMPRINT",EDGE,{"disambiguationData":[TD([[subQ3,-1.0]])],"derivedFrom":subQ0}),1.0]])]});}
            extrude(context, id + "F39", {"entities" : qUnion([Q0, Q1, Q2, Q3, Q4, Q5, Q6, Q7, Q8, Q9]), "operationType" : NewBodyOperationType.REMOVE, "oppositeDirection" : true, "depth" : 5 * mm, "offsetDistance" : 25 * mm, "hasDraft" : true, "draftAngle" : 45 * degree, "draftPullDirection" : true});
        }
        {
            var Q0;
            Q0=makeQuery(id+"F20.opRevolve","SWEPT_FACE",FACE,{"disambiguationData":[OSD([sQuery(id+"F19.wireOp",EDGE,"E30")])]});
            var sketch = newSketch(context, id + "F40", { "sketchPlane" : qUnion([Q0])});
            skLineSegment(sketch, "E192", {"start": v(-0.01, 0.04) * mm, "end": v(32.49, 0.04) * mm});
            skLineSegment(sketch, "E193.1.0", {"start": v(-0.01, 0.04) * mm, "end": v(19.02, 6.23) * mm});
            skLineSegment(sketch, "E193.2.0", {"start": v(-0.01, 0.04) * mm, "end": v(16.18, 11.8) * mm});
            skLineSegment(sketch, "E193.3.0", {"start": v(-0.01, 0.04) * mm, "end": v(19.09, 26.33) * mm});
            skLineSegment(sketch, "E193.4.0", {"start": v(-0.01, 0.04) * mm, "end": v(10.03, 30.95) * mm});
            skLineSegment(sketch, "E193.5.0", {"start": v(-0.01, 0.04) * mm, "end": v(-0.01, 32.54) * mm});
            skLineSegment(sketch, "E193.6.0", {"start": v(-0.01, 0.04) * mm, "end": v(-10.06, 30.95) * mm});
            skLineSegment(sketch, "E193.7.0", {"start": v(-0.01, 0.04) * mm, "end": v(-19.12, 26.33) * mm});
            skLineSegment(sketch, "E193.8.0", {"start": v(-0.01, 0.04) * mm, "end": v(-26.3, 19.14) * mm});
            skLineSegment(sketch, "E193.9.0", {"start": v(-0.01, 0.04) * mm, "end": v(-19.05, 6.23) * mm});
            skLineSegment(sketch, "E193.10.0", {"start": v(-0.01, 0.04) * mm, "end": v(-32.51, 0.04) * mm});
            skLineSegment(sketch, "E193.11.0", {"start": v(-0.01, 0.04) * mm, "end": v(-30.92, -10) * mm});
            skLineSegment(sketch, "E193.12.0", {"start": v(-0.01, 0.04) * mm, "end": v(-16.2, -11.72) * mm});
            skLineSegment(sketch, "E193.13.0", {"start": v(-0.01, 0.04) * mm, "end": v(-19.12, -26.25) * mm});
            skLineSegment(sketch, "E193.14.0", {"start": v(-0.01, 0.04) * mm, "end": v(-6.2, -19) * mm});
            skLineSegment(sketch, "E193.15.0", {"start": v(-0.01, 0.04) * mm, "end": v(-0.01, -19.97) * mm});
            skLineSegment(sketch, "E193.16.0", {"start": v(-0.01, 0.04) * mm, "end": v(6.17, -19) * mm});
            skLineSegment(sketch, "E193.17.0", {"start": v(-0.01, 0.04) * mm, "end": v(19.09, -26.25) * mm});
            skLineSegment(sketch, "E193.18.0", {"start": v(-0.01, 0.04) * mm, "end": v(16.18, -11.72) * mm});
            skLineSegment(sketch, "E193.19.0", {"start": v(-0.01, 0.04) * mm, "end": v(30.9, -10) * mm});
            skPoint(sketch, "E193.center", {"position": v(-0.01, 0.04) * mm});
            skCircle(sketch, "E194", {"center": v(-0.01, 0.04) * mm, "radius": 32.5 * mm});
            skArc(sketch, "E195", {"start": v(-16.2, 11.8) * mm, "mid": v(-19.05, 6.23) * mm, "end": v(-20.03, 0.04) * mm});
            skArc(sketch, "E196", {"start": v(-11.78, 16.23) * mm, "mid": v(-14.17, 14.2) * mm, "end": v(-16.2, 11.8) * mm});
            skArc(sketch, "E197", {"start": v(-6.2, 19.08) * mm, "mid": v(-9.1, 17.87) * mm, "end": v(-11.78, 16.23) * mm});
            skArc(sketch, "E198", {"start": v(-0.01, 20.06) * mm, "mid": v(-3.14, 19.81) * mm, "end": v(-6.2, 19.08) * mm});
            skArc(sketch, "E199", {"start": v(6.17, 19.08) * mm, "mid": v(3.12, 19.81) * mm, "end": v(-0.01, 20.06) * mm});
            skArc(sketch, "E200", {"start": v(11.75, 16.23) * mm, "mid": v(9.07, 17.87) * mm, "end": v(6.17, 19.08) * mm});
            skLineSegment(sketch, "E201", {"start": v(16.18, 11.8) * mm, "end": v(26.28, 19.14) * mm});
            skLineSegment(sketch, "E202", {"start": v(19.02, 6.23) * mm, "end": v(30.9, 10.08) * mm});
            skArc(sketch, "E203", {"start": v(20, 0.04) * mm, "mid": v(17.82, 9.13) * mm, "end": v(11.75, 16.23) * mm});
            skArc(sketch, "E204", {"start": v(19.02, -6.14) * mm, "mid": v(19.75, -3.09) * mm, "end": v(20, 0.04) * mm});
            skLineSegment(sketch, "E205", {"start": v(16.18, -11.72) * mm, "end": v(26.28, -19.06) * mm});
            skArc(sketch, "E206", {"start": v(11.75, -16.15) * mm, "mid": v(16.18, -11.72) * mm, "end": v(19.02, -6.14) * mm});
            skLineSegment(sketch, "E207", {"start": v(6.17, -19) * mm, "end": v(10.03, -30.87) * mm});
            skLineSegment(sketch, "E208", {"start": v(-0.01, -19.97) * mm, "end": v(-0.01, -32.46) * mm});
            skLineSegment(sketch, "E209", {"start": v(-6.2, -19) * mm, "end": v(-10.06, -30.87) * mm});
            skArc(sketch, "E210", {"start": v(-11.78, -16.15) * mm, "mid": v(-0.01, -19.97) * mm, "end": v(11.75, -16.15) * mm});
            skLineSegment(sketch, "E211", {"start": v(-16.2, -11.72) * mm, "end": v(-26.3, -19.06) * mm});
            skArc(sketch, "E212", {"start": v(-19.05, -6.14) * mm, "mid": v(-16.2, -11.72) * mm, "end": v(-11.78, -16.15) * mm});
            skArc(sketch, "E213", {"start": v(-20.03, 0.04) * mm, "mid": v(-19.78, -3.09) * mm, "end": v(-19.05, -6.14) * mm});
            skLineSegment(sketch, "E214", {"start": v(-19.05, 6.23) * mm, "end": v(-30.92, 10.08) * mm});
            skSolve(sketch);
        }
        {
            var Q0;
            {var subQ0=sQuery(id+"F40.wireOp",EDGE,"E193.12.0");var subQ1=sQuery(id+"F19.wireOp",EDGE,"E30");var subQ2=makeQuery(id+"F20.opRevolve","SWEPT_EDGE",EDGE,{"disambiguationData":[OSD([sQuery(id+"F19.wireOp",EDGE,"E29"),subQ1])]});var subQ3=makeQuery(id+"F40.imprint","INTERSECT",VERTEX,{"derivedFrom":[subQ2,subQ0]});Q0=makeQuery(id+"F40.imprint","IMPRINT",FACE,{"disambiguationData":[TD([[makeQuery(id+"F40.imprint","IMPRINT",EDGE,{"disambiguationData":[TD([[subQ3,-1.0]])],"derivedFrom":subQ0}),1.0]])]});}
            var Q1;
            {var subQ0=sQuery(id+"F40.wireOp",EDGE,"E193.14.0");var subQ1=sQuery(id+"F19.wireOp",EDGE,"E30");var subQ2=makeQuery(id+"F20.opRevolve","SWEPT_EDGE",EDGE,{"disambiguationData":[OSD([sQuery(id+"F19.wireOp",EDGE,"E29"),subQ1])]});var subQ3=makeQuery(id+"F40.imprint","INTERSECT",VERTEX,{"derivedFrom":[subQ2,subQ0]});Q1=makeQuery(id+"F40.imprint","IMPRINT",FACE,{"disambiguationData":[TD([[makeQuery(id+"F40.imprint","IMPRINT",EDGE,{"disambiguationData":[TD([[subQ3,-1.0]])],"derivedFrom":subQ0}),1.0]])]});}
            var Q2;
            {var subQ0=sQuery(id+"F40.wireOp",EDGE,"E193.16.0");var subQ1=sQuery(id+"F19.wireOp",EDGE,"E30");var subQ2=makeQuery(id+"F20.opRevolve","SWEPT_EDGE",EDGE,{"disambiguationData":[OSD([sQuery(id+"F19.wireOp",EDGE,"E29"),subQ1])]});var subQ3=makeQuery(id+"F40.imprint","INTERSECT",VERTEX,{"derivedFrom":[subQ2,subQ0]});Q2=makeQuery(id+"F40.imprint","IMPRINT",FACE,{"disambiguationData":[TD([[makeQuery(id+"F40.imprint","IMPRINT",EDGE,{"disambiguationData":[TD([[subQ3,-1.0]])],"derivedFrom":subQ0}),1.0]])]});}
            var Q3;
            {var subQ0=sQuery(id+"F40.wireOp",EDGE,"E193.18.0");var subQ1=sQuery(id+"F19.wireOp",EDGE,"E30");var subQ2=makeQuery(id+"F20.opRevolve","SWEPT_EDGE",EDGE,{"disambiguationData":[OSD([sQuery(id+"F19.wireOp",EDGE,"E29"),subQ1])]});var subQ3=makeQuery(id+"F40.imprint","INTERSECT",VERTEX,{"derivedFrom":[subQ2,subQ0]});Q3=makeQuery(id+"F40.imprint","IMPRINT",FACE,{"disambiguationData":[TD([[makeQuery(id+"F40.imprint","IMPRINT",EDGE,{"disambiguationData":[TD([[subQ3,-1.0]])],"derivedFrom":subQ0}),1.0]])]});}
            var Q4;
            {var subQ0=sQuery(id+"F40.wireOp",EDGE,"E192");var subQ1=sQuery(id+"F19.wireOp",EDGE,"E30");var subQ2=makeQuery(id+"F20.opRevolve","SWEPT_EDGE",EDGE,{"disambiguationData":[OSD([sQuery(id+"F19.wireOp",EDGE,"E29"),subQ1])]});var subQ3=makeQuery(id+"F40.imprint","INTERSECT",VERTEX,{"derivedFrom":[subQ2,subQ0]});Q4=makeQuery(id+"F40.imprint","IMPRINT",FACE,{"disambiguationData":[TD([[makeQuery(id+"F40.imprint","IMPRINT",EDGE,{"disambiguationData":[TD([[subQ3,-1.0]])],"derivedFrom":subQ0}),1.0]])]});}
            var Q5;
            {var subQ0=sQuery(id+"F40.wireOp",EDGE,"E193.2.0");var subQ1=sQuery(id+"F19.wireOp",EDGE,"E30");var subQ2=makeQuery(id+"F20.opRevolve","SWEPT_EDGE",EDGE,{"disambiguationData":[OSD([sQuery(id+"F19.wireOp",EDGE,"E29"),subQ1])]});var subQ3=makeQuery(id+"F40.imprint","INTERSECT",VERTEX,{"derivedFrom":[subQ2,subQ0]});Q5=makeQuery(id+"F40.imprint","IMPRINT",FACE,{"disambiguationData":[TD([[makeQuery(id+"F40.imprint","IMPRINT",EDGE,{"disambiguationData":[TD([[subQ3,-1.0]])],"derivedFrom":subQ0}),1.0]])]});}
            var Q6;
            {var subQ0=sQuery(id+"F40.wireOp",EDGE,"E193.4.0");var subQ1=sQuery(id+"F19.wireOp",EDGE,"E30");var subQ2=makeQuery(id+"F20.opRevolve","SWEPT_EDGE",EDGE,{"disambiguationData":[OSD([sQuery(id+"F19.wireOp",EDGE,"E29"),subQ1])]});var subQ3=makeQuery(id+"F40.imprint","INTERSECT",VERTEX,{"derivedFrom":[subQ2,subQ0]});Q6=makeQuery(id+"F40.imprint","IMPRINT",FACE,{"disambiguationData":[TD([[makeQuery(id+"F40.imprint","IMPRINT",EDGE,{"disambiguationData":[TD([[subQ3,-1.0]])],"derivedFrom":subQ0}),1.0]])]});}
            var Q7;
            {var subQ0=sQuery(id+"F40.wireOp",EDGE,"E193.6.0");var subQ1=sQuery(id+"F19.wireOp",EDGE,"E30");var subQ2=makeQuery(id+"F20.opRevolve","SWEPT_EDGE",EDGE,{"disambiguationData":[OSD([sQuery(id+"F19.wireOp",EDGE,"E29"),subQ1])]});var subQ3=makeQuery(id+"F40.imprint","INTERSECT",VERTEX,{"derivedFrom":[subQ2,subQ0]});Q7=makeQuery(id+"F40.imprint","IMPRINT",FACE,{"disambiguationData":[TD([[makeQuery(id+"F40.imprint","IMPRINT",EDGE,{"disambiguationData":[TD([[subQ3,-1.0]])],"derivedFrom":subQ0}),1.0]])]});}
            var Q8;
            {var subQ0=sQuery(id+"F40.wireOp",EDGE,"E193.8.0");var subQ1=sQuery(id+"F19.wireOp",EDGE,"E30");var subQ2=makeQuery(id+"F20.opRevolve","SWEPT_EDGE",EDGE,{"disambiguationData":[OSD([sQuery(id+"F19.wireOp",EDGE,"E29"),subQ1])]});var subQ3=makeQuery(id+"F40.imprint","INTERSECT",VERTEX,{"derivedFrom":[subQ2,subQ0]});Q8=makeQuery(id+"F40.imprint","IMPRINT",FACE,{"disambiguationData":[TD([[makeQuery(id+"F40.imprint","IMPRINT",EDGE,{"disambiguationData":[TD([[subQ3,-1.0]])],"derivedFrom":subQ0}),1.0]])]});}
            var Q9;
            {var subQ0=sQuery(id+"F40.wireOp",EDGE,"E193.10.0");var subQ1=sQuery(id+"F19.wireOp",EDGE,"E30");var subQ2=makeQuery(id+"F20.opRevolve","SWEPT_EDGE",EDGE,{"disambiguationData":[OSD([sQuery(id+"F19.wireOp",EDGE,"E29"),subQ1])]});var subQ3=makeQuery(id+"F40.imprint","INTERSECT",VERTEX,{"derivedFrom":[subQ2,subQ0]});Q9=makeQuery(id+"F40.imprint","IMPRINT",FACE,{"disambiguationData":[TD([[makeQuery(id+"F40.imprint","IMPRINT",EDGE,{"disambiguationData":[TD([[subQ3,-1.0]])],"derivedFrom":subQ0}),1.0]])]});}
            extrude(context, id + "F41", {"entities" : qUnion([Q0, Q1, Q2, Q3, Q4, Q5, Q6, Q7, Q8, Q9]), "operationType" : NewBodyOperationType.REMOVE, "oppositeDirection" : true, "depth" : 5 * mm, "offsetDistance" : 25 * mm, "hasDraft" : true, "draftAngle" : 45 * degree, "draftPullDirection" : true});
        }
        {
            var Q0;
            {var subQ0=sQuery(id+"F40.wireOp",EDGE,"E193.9.0");var subQ1=sQuery(id+"F19.wireOp",EDGE,"E30");var subQ2=makeQuery(id+"F20.opRevolve","SWEPT_EDGE",EDGE,{"disambiguationData":[OSD([sQuery(id+"F19.wireOp",EDGE,"E29"),subQ1])]});var subQ3=makeQuery(id+"F40.imprint","INTERSECT",VERTEX,{"derivedFrom":[subQ2,subQ0]});Q0=makeQuery(id+"F40.imprint","IMPRINT",FACE,{"disambiguationData":[TD([[makeQuery(id+"F40.imprint","IMPRINT",EDGE,{"disambiguationData":[TD([[subQ3,-1.0]])],"derivedFrom":subQ0}),1.0]])]});}
            var Q1;
            {var subQ0=sQuery(id+"F40.wireOp",EDGE,"E193.7.0");var subQ1=sQuery(id+"F19.wireOp",EDGE,"E30");var subQ2=makeQuery(id+"F20.opRevolve","SWEPT_EDGE",EDGE,{"disambiguationData":[OSD([sQuery(id+"F19.wireOp",EDGE,"E29"),subQ1])]});var subQ3=makeQuery(id+"F40.imprint","INTERSECT",VERTEX,{"derivedFrom":[subQ2,subQ0]});Q1=makeQuery(id+"F40.imprint","IMPRINT",FACE,{"disambiguationData":[TD([[makeQuery(id+"F40.imprint","IMPRINT",EDGE,{"disambiguationData":[TD([[subQ3,-1.0]])],"derivedFrom":subQ0}),1.0]])]});}
            var Q2;
            {var subQ0=sQuery(id+"F40.wireOp",EDGE,"E193.5.0");var subQ1=sQuery(id+"F19.wireOp",EDGE,"E30");var subQ2=makeQuery(id+"F20.opRevolve","SWEPT_EDGE",EDGE,{"disambiguationData":[OSD([sQuery(id+"F19.wireOp",EDGE,"E29"),subQ1])]});var subQ3=makeQuery(id+"F40.imprint","INTERSECT",VERTEX,{"derivedFrom":[subQ2,subQ0]});Q2=makeQuery(id+"F40.imprint","IMPRINT",FACE,{"disambiguationData":[TD([[makeQuery(id+"F40.imprint","IMPRINT",EDGE,{"disambiguationData":[TD([[subQ3,-1.0]])],"derivedFrom":subQ0}),1.0]])]});}
            var Q3;
            {var subQ0=sQuery(id+"F40.wireOp",EDGE,"E193.3.0");var subQ1=sQuery(id+"F19.wireOp",EDGE,"E30");var subQ2=makeQuery(id+"F20.opRevolve","SWEPT_EDGE",EDGE,{"disambiguationData":[OSD([sQuery(id+"F19.wireOp",EDGE,"E29"),subQ1])]});var subQ3=makeQuery(id+"F40.imprint","INTERSECT",VERTEX,{"derivedFrom":[subQ2,subQ0]});Q3=makeQuery(id+"F40.imprint","IMPRINT",FACE,{"disambiguationData":[TD([[makeQuery(id+"F40.imprint","IMPRINT",EDGE,{"disambiguationData":[TD([[subQ3,-1.0]])],"derivedFrom":subQ0}),1.0]])]});}
            var Q4;
            {var subQ0=sQuery(id+"F40.wireOp",EDGE,"E193.1.0");var subQ1=sQuery(id+"F19.wireOp",EDGE,"E30");var subQ2=makeQuery(id+"F20.opRevolve","SWEPT_EDGE",EDGE,{"disambiguationData":[OSD([sQuery(id+"F19.wireOp",EDGE,"E29"),subQ1])]});var subQ3=makeQuery(id+"F40.imprint","INTERSECT",VERTEX,{"derivedFrom":[subQ2,subQ0]});Q4=makeQuery(id+"F40.imprint","IMPRINT",FACE,{"disambiguationData":[TD([[makeQuery(id+"F40.imprint","IMPRINT",EDGE,{"disambiguationData":[TD([[subQ3,-1.0]])],"derivedFrom":subQ0}),1.0]])]});}
            var Q5;
            {var subQ0=sQuery(id+"F40.wireOp",EDGE,"E192");var subQ1=sQuery(id+"F19.wireOp",EDGE,"E30");var subQ2=makeQuery(id+"F20.opRevolve","SWEPT_EDGE",EDGE,{"disambiguationData":[OSD([sQuery(id+"F19.wireOp",EDGE,"E29"),subQ1])]});var subQ3=makeQuery(id+"F40.imprint","INTERSECT",VERTEX,{"derivedFrom":[subQ2,subQ0]});Q5=makeQuery(id+"F40.imprint","IMPRINT",FACE,{"disambiguationData":[TD([[makeQuery(id+"F40.imprint","IMPRINT",EDGE,{"disambiguationData":[TD([[subQ3,-1.0]])],"derivedFrom":subQ0}),-1.0]])]});}
            var Q6;
            {var subQ0=sQuery(id+"F40.wireOp",EDGE,"E193.17.0");var subQ1=sQuery(id+"F19.wireOp",EDGE,"E30");var subQ2=makeQuery(id+"F20.opRevolve","SWEPT_EDGE",EDGE,{"disambiguationData":[OSD([sQuery(id+"F19.wireOp",EDGE,"E29"),subQ1])]});var subQ3=makeQuery(id+"F40.imprint","INTERSECT",VERTEX,{"derivedFrom":[subQ2,subQ0]});Q6=makeQuery(id+"F40.imprint","IMPRINT",FACE,{"disambiguationData":[TD([[makeQuery(id+"F40.imprint","IMPRINT",EDGE,{"disambiguationData":[TD([[subQ3,-1.0]])],"derivedFrom":subQ0}),1.0]])]});}
            var Q7;
            {var subQ0=sQuery(id+"F40.wireOp",EDGE,"E193.15.0");var subQ1=sQuery(id+"F19.wireOp",EDGE,"E30");var subQ2=makeQuery(id+"F20.opRevolve","SWEPT_EDGE",EDGE,{"disambiguationData":[OSD([sQuery(id+"F19.wireOp",EDGE,"E29"),subQ1])]});var subQ3=makeQuery(id+"F40.imprint","INTERSECT",VERTEX,{"derivedFrom":[subQ2,subQ0]});Q7=makeQuery(id+"F40.imprint","IMPRINT",FACE,{"disambiguationData":[TD([[makeQuery(id+"F40.imprint","IMPRINT",EDGE,{"disambiguationData":[TD([[subQ3,-1.0]])],"derivedFrom":subQ0}),1.0]])]});}
            var Q8;
            {var subQ0=sQuery(id+"F40.wireOp",EDGE,"E193.13.0");var subQ1=sQuery(id+"F19.wireOp",EDGE,"E30");var subQ2=makeQuery(id+"F20.opRevolve","SWEPT_EDGE",EDGE,{"disambiguationData":[OSD([sQuery(id+"F19.wireOp",EDGE,"E29"),subQ1])]});var subQ3=makeQuery(id+"F40.imprint","INTERSECT",VERTEX,{"derivedFrom":[subQ2,subQ0]});Q8=makeQuery(id+"F40.imprint","IMPRINT",FACE,{"disambiguationData":[TD([[makeQuery(id+"F40.imprint","IMPRINT",EDGE,{"disambiguationData":[TD([[subQ3,-1.0]])],"derivedFrom":subQ0}),1.0]])]});}
            var Q9;
            {var subQ0=sQuery(id+"F40.wireOp",EDGE,"E193.11.0");var subQ1=sQuery(id+"F19.wireOp",EDGE,"E30");var subQ2=makeQuery(id+"F20.opRevolve","SWEPT_EDGE",EDGE,{"disambiguationData":[OSD([sQuery(id+"F19.wireOp",EDGE,"E29"),subQ1])]});var subQ3=makeQuery(id+"F40.imprint","INTERSECT",VERTEX,{"derivedFrom":[subQ2,subQ0]});Q9=makeQuery(id+"F40.imprint","IMPRINT",FACE,{"disambiguationData":[TD([[makeQuery(id+"F40.imprint","IMPRINT",EDGE,{"disambiguationData":[TD([[subQ3,-1.0]])],"derivedFrom":subQ0}),1.0]])]});}
            extrude(context, id + "F42", {"entities" : qUnion([Q0, Q1, Q2, Q3, Q4, Q5, Q6, Q7, Q8, Q9]), "operationType" : NewBodyOperationType.REMOVE, "oppositeDirection" : true, "depth" : 5 * mm, "offsetDistance" : 25 * mm, "hasDraft" : true, "draftAngle" : 45 * degree, "draftPullDirection" : true});
        }
        {
            var Q0;
            Q0=makeQuery(id+"F25.opRevolve","SWEPT_FACE",FACE,{"disambiguationData":[OSD([sQuery(id+"F24.wireOp",EDGE,"E105")])]});
            var sketch = newSketch(context, id + "F43", { "sketchPlane" : qUnion([Q0])});
            skLineSegment(sketch, "E215", {"start": v(-0.01, 0.04) * mm, "end": v(32.49, 0.04) * mm});
            skLineSegment(sketch, "E216.1.0", {"start": v(-0.01, 0.04) * mm, "end": v(19.02, 6.23) * mm});
            skLineSegment(sketch, "E216.2.0", {"start": v(-0.01, 0.04) * mm, "end": v(16.18, 11.8) * mm});
            skLineSegment(sketch, "E216.3.0", {"start": v(-0.01, 0.04) * mm, "end": v(19.09, 26.33) * mm});
            skLineSegment(sketch, "E216.4.0", {"start": v(-0.01, 0.04) * mm, "end": v(10.03, 30.95) * mm});
            skLineSegment(sketch, "E216.5.0", {"start": v(-0.01, 0.04) * mm, "end": v(-0.01, 32.54) * mm});
            skLineSegment(sketch, "E216.6.0", {"start": v(-0.01, 0.04) * mm, "end": v(-10.06, 30.95) * mm});
            skLineSegment(sketch, "E216.7.0", {"start": v(-0.01, 0.04) * mm, "end": v(-19.12, 26.33) * mm});
            skLineSegment(sketch, "E216.8.0", {"start": v(-0.01, 0.04) * mm, "end": v(-26.3, 19.14) * mm});
            skLineSegment(sketch, "E216.9.0", {"start": v(-0.01, 0.04) * mm, "end": v(-19.05, 6.23) * mm});
            skLineSegment(sketch, "E216.10.0", {"start": v(-0.01, 0.04) * mm, "end": v(-32.51, 0.04) * mm});
            skLineSegment(sketch, "E216.11.0", {"start": v(-0.01, 0.04) * mm, "end": v(-30.92, -10) * mm});
            skLineSegment(sketch, "E216.12.0", {"start": v(-0.01, 0.04) * mm, "end": v(-16.2, -11.72) * mm});
            skLineSegment(sketch, "E216.13.0", {"start": v(-0.01, 0.04) * mm, "end": v(-19.12, -26.25) * mm});
            skLineSegment(sketch, "E216.14.0", {"start": v(-0.01, 0.04) * mm, "end": v(-6.2, -19) * mm});
            skLineSegment(sketch, "E216.15.0", {"start": v(-0.01, 0.04) * mm, "end": v(-0.01, -19.97) * mm});
            skLineSegment(sketch, "E216.16.0", {"start": v(-0.01, 0.04) * mm, "end": v(6.17, -19) * mm});
            skLineSegment(sketch, "E216.17.0", {"start": v(-0.01, 0.04) * mm, "end": v(19.09, -26.25) * mm});
            skLineSegment(sketch, "E216.18.0", {"start": v(-0.01, 0.04) * mm, "end": v(16.18, -11.72) * mm});
            skLineSegment(sketch, "E216.19.0", {"start": v(-0.01, 0.04) * mm, "end": v(30.9, -10) * mm});
            skPoint(sketch, "E216.center", {"position": v(-0.01, 0.04) * mm});
            skCircle(sketch, "E217", {"center": v(-0.01, 0.04) * mm, "radius": 32.5 * mm});
            skArc(sketch, "E218", {"start": v(-16.2, 11.8) * mm, "mid": v(-19.05, 6.23) * mm, "end": v(-20.03, 0.04) * mm});
            skArc(sketch, "E219", {"start": v(-11.78, 16.23) * mm, "mid": v(-14.17, 14.2) * mm, "end": v(-16.2, 11.8) * mm});
            skArc(sketch, "E220", {"start": v(-6.2, 19.08) * mm, "mid": v(-9.1, 17.87) * mm, "end": v(-11.78, 16.23) * mm});
            skArc(sketch, "E221", {"start": v(-0.01, 20.06) * mm, "mid": v(-3.14, 19.81) * mm, "end": v(-6.2, 19.08) * mm});
            skArc(sketch, "E222", {"start": v(6.17, 19.08) * mm, "mid": v(3.12, 19.81) * mm, "end": v(-0.01, 20.06) * mm});
            skArc(sketch, "E223", {"start": v(11.75, 16.23) * mm, "mid": v(9.07, 17.87) * mm, "end": v(6.17, 19.08) * mm});
            skLineSegment(sketch, "E224", {"start": v(16.18, 11.8) * mm, "end": v(26.28, 19.14) * mm});
            skLineSegment(sketch, "E225", {"start": v(19.02, 6.23) * mm, "end": v(30.9, 10.08) * mm});
            skArc(sketch, "E226", {"start": v(20, 0.04) * mm, "mid": v(17.82, 9.13) * mm, "end": v(11.75, 16.23) * mm});
            skArc(sketch, "E227", {"start": v(19.02, -6.14) * mm, "mid": v(19.75, -3.09) * mm, "end": v(20, 0.04) * mm});
            skLineSegment(sketch, "E228", {"start": v(16.18, -11.72) * mm, "end": v(26.28, -19.06) * mm});
            skArc(sketch, "E229", {"start": v(11.75, -16.15) * mm, "mid": v(16.18, -11.72) * mm, "end": v(19.02, -6.14) * mm});
            skLineSegment(sketch, "E230", {"start": v(6.17, -19) * mm, "end": v(10.03, -30.87) * mm});
            skLineSegment(sketch, "E231", {"start": v(-0.01, -19.97) * mm, "end": v(-0.01, -32.46) * mm});
            skLineSegment(sketch, "E232", {"start": v(-6.2, -19) * mm, "end": v(-10.06, -30.87) * mm});
            skArc(sketch, "E233", {"start": v(-11.78, -16.15) * mm, "mid": v(-0.01, -19.97) * mm, "end": v(11.75, -16.15) * mm});
            skLineSegment(sketch, "E234", {"start": v(-16.2, -11.72) * mm, "end": v(-26.3, -19.06) * mm});
            skArc(sketch, "E235", {"start": v(-19.05, -6.14) * mm, "mid": v(-16.2, -11.72) * mm, "end": v(-11.78, -16.15) * mm});
            skArc(sketch, "E236", {"start": v(-20.03, 0.04) * mm, "mid": v(-19.78, -3.09) * mm, "end": v(-19.05, -6.14) * mm});
            skLineSegment(sketch, "E237", {"start": v(-19.05, 6.23) * mm, "end": v(-30.92, 10.08) * mm});
            skSolve(sketch);
        }
        {
            var Q0;
            {var subQ0=sQuery(id+"F43.wireOp",EDGE,"E215");var subQ1=sQuery(id+"F24.wireOp",EDGE,"E105");var subQ2=makeQuery(id+"F25.opRevolve","SWEPT_EDGE",EDGE,{"disambiguationData":[OSD([subQ1,sQuery(id+"F24.wireOp",EDGE,"E106")])]});var subQ3=makeQuery(id+"F43.imprint","INTERSECT",VERTEX,{"derivedFrom":[subQ2,subQ0]});Q0=makeQuery(id+"F43.imprint","IMPRINT",FACE,{"disambiguationData":[TD([[makeQuery(id+"F43.imprint","IMPRINT",EDGE,{"disambiguationData":[TD([[subQ3,-1.0]])],"derivedFrom":subQ0}),1.0]])]});}
            var Q1;
            {var subQ0=sQuery(id+"F43.wireOp",EDGE,"E216.2.0");var subQ1=sQuery(id+"F24.wireOp",EDGE,"E105");var subQ2=makeQuery(id+"F25.opRevolve","SWEPT_EDGE",EDGE,{"disambiguationData":[OSD([subQ1,sQuery(id+"F24.wireOp",EDGE,"E106")])]});var subQ3=makeQuery(id+"F43.imprint","INTERSECT",VERTEX,{"derivedFrom":[subQ2,subQ0]});Q1=makeQuery(id+"F43.imprint","IMPRINT",FACE,{"disambiguationData":[TD([[makeQuery(id+"F43.imprint","IMPRINT",EDGE,{"disambiguationData":[TD([[subQ3,-1.0]])],"derivedFrom":subQ0}),1.0]])]});}
            var Q2;
            {var subQ0=sQuery(id+"F43.wireOp",EDGE,"E216.4.0");var subQ1=sQuery(id+"F24.wireOp",EDGE,"E105");var subQ2=makeQuery(id+"F25.opRevolve","SWEPT_EDGE",EDGE,{"disambiguationData":[OSD([subQ1,sQuery(id+"F24.wireOp",EDGE,"E106")])]});var subQ3=makeQuery(id+"F43.imprint","INTERSECT",VERTEX,{"derivedFrom":[subQ2,subQ0]});Q2=makeQuery(id+"F43.imprint","IMPRINT",FACE,{"disambiguationData":[TD([[makeQuery(id+"F43.imprint","IMPRINT",EDGE,{"disambiguationData":[TD([[subQ3,-1.0]])],"derivedFrom":subQ0}),1.0]])]});}
            var Q3;
            {var subQ0=sQuery(id+"F43.wireOp",EDGE,"E216.6.0");var subQ1=sQuery(id+"F24.wireOp",EDGE,"E105");var subQ2=makeQuery(id+"F25.opRevolve","SWEPT_EDGE",EDGE,{"disambiguationData":[OSD([subQ1,sQuery(id+"F24.wireOp",EDGE,"E106")])]});var subQ3=makeQuery(id+"F43.imprint","INTERSECT",VERTEX,{"derivedFrom":[subQ2,subQ0]});Q3=makeQuery(id+"F43.imprint","IMPRINT",FACE,{"disambiguationData":[TD([[makeQuery(id+"F43.imprint","IMPRINT",EDGE,{"disambiguationData":[TD([[subQ3,-1.0]])],"derivedFrom":subQ0}),1.0]])]});}
            var Q4;
            {var subQ0=sQuery(id+"F43.wireOp",EDGE,"E216.8.0");var subQ1=sQuery(id+"F24.wireOp",EDGE,"E105");var subQ2=makeQuery(id+"F25.opRevolve","SWEPT_EDGE",EDGE,{"disambiguationData":[OSD([subQ1,sQuery(id+"F24.wireOp",EDGE,"E106")])]});var subQ3=makeQuery(id+"F43.imprint","INTERSECT",VERTEX,{"derivedFrom":[subQ2,subQ0]});Q4=makeQuery(id+"F43.imprint","IMPRINT",FACE,{"disambiguationData":[TD([[makeQuery(id+"F43.imprint","IMPRINT",EDGE,{"disambiguationData":[TD([[subQ3,-1.0]])],"derivedFrom":subQ0}),1.0]])]});}
            var Q5;
            {var subQ0=sQuery(id+"F43.wireOp",EDGE,"E216.10.0");var subQ1=sQuery(id+"F24.wireOp",EDGE,"E105");var subQ2=makeQuery(id+"F25.opRevolve","SWEPT_EDGE",EDGE,{"disambiguationData":[OSD([subQ1,sQuery(id+"F24.wireOp",EDGE,"E106")])]});var subQ3=makeQuery(id+"F43.imprint","INTERSECT",VERTEX,{"derivedFrom":[subQ2,subQ0]});Q5=makeQuery(id+"F43.imprint","IMPRINT",FACE,{"disambiguationData":[TD([[makeQuery(id+"F43.imprint","IMPRINT",EDGE,{"disambiguationData":[TD([[subQ3,-1.0]])],"derivedFrom":subQ0}),1.0]])]});}
            var Q6;
            {var subQ0=sQuery(id+"F43.wireOp",EDGE,"E216.12.0");var subQ1=sQuery(id+"F24.wireOp",EDGE,"E105");var subQ2=makeQuery(id+"F25.opRevolve","SWEPT_EDGE",EDGE,{"disambiguationData":[OSD([subQ1,sQuery(id+"F24.wireOp",EDGE,"E106")])]});var subQ3=makeQuery(id+"F43.imprint","INTERSECT",VERTEX,{"derivedFrom":[subQ2,subQ0]});Q6=makeQuery(id+"F43.imprint","IMPRINT",FACE,{"disambiguationData":[TD([[makeQuery(id+"F43.imprint","IMPRINT",EDGE,{"disambiguationData":[TD([[subQ3,-1.0]])],"derivedFrom":subQ0}),1.0]])]});}
            var Q7;
            {var subQ0=sQuery(id+"F43.wireOp",EDGE,"E216.14.0");var subQ1=sQuery(id+"F24.wireOp",EDGE,"E105");var subQ2=makeQuery(id+"F25.opRevolve","SWEPT_EDGE",EDGE,{"disambiguationData":[OSD([subQ1,sQuery(id+"F24.wireOp",EDGE,"E106")])]});var subQ3=makeQuery(id+"F43.imprint","INTERSECT",VERTEX,{"derivedFrom":[subQ2,subQ0]});Q7=makeQuery(id+"F43.imprint","IMPRINT",FACE,{"disambiguationData":[TD([[makeQuery(id+"F43.imprint","IMPRINT",EDGE,{"disambiguationData":[TD([[subQ3,-1.0]])],"derivedFrom":subQ0}),1.0]])]});}
            var Q8;
            {var subQ0=sQuery(id+"F43.wireOp",EDGE,"E216.16.0");var subQ1=sQuery(id+"F24.wireOp",EDGE,"E105");var subQ2=makeQuery(id+"F25.opRevolve","SWEPT_EDGE",EDGE,{"disambiguationData":[OSD([subQ1,sQuery(id+"F24.wireOp",EDGE,"E106")])]});var subQ3=makeQuery(id+"F43.imprint","INTERSECT",VERTEX,{"derivedFrom":[subQ2,subQ0]});Q8=makeQuery(id+"F43.imprint","IMPRINT",FACE,{"disambiguationData":[TD([[makeQuery(id+"F43.imprint","IMPRINT",EDGE,{"disambiguationData":[TD([[subQ3,-1.0]])],"derivedFrom":subQ0}),1.0]])]});}
            var Q9;
            {var subQ0=sQuery(id+"F43.wireOp",EDGE,"E216.18.0");var subQ1=sQuery(id+"F24.wireOp",EDGE,"E105");var subQ2=makeQuery(id+"F25.opRevolve","SWEPT_EDGE",EDGE,{"disambiguationData":[OSD([subQ1,sQuery(id+"F24.wireOp",EDGE,"E106")])]});var subQ3=makeQuery(id+"F43.imprint","INTERSECT",VERTEX,{"derivedFrom":[subQ2,subQ0]});Q9=makeQuery(id+"F43.imprint","IMPRINT",FACE,{"disambiguationData":[TD([[makeQuery(id+"F43.imprint","IMPRINT",EDGE,{"disambiguationData":[TD([[subQ3,-1.0]])],"derivedFrom":subQ0}),1.0]])]});}
            extrude(context, id + "F44", {"entities" : qUnion([Q0, Q1, Q2, Q3, Q4, Q5, Q6, Q7, Q8, Q9]), "operationType" : NewBodyOperationType.REMOVE, "oppositeDirection" : true, "depth" : 3 * mm, "offsetDistance" : 25 * mm, "hasDraft" : true, "draftAngle" : 45 * degree, "draftPullDirection" : true});
        }
        {
            var Q0;
            {var subQ0=sQuery(id+"F43.wireOp",EDGE,"E216.1.0");var subQ1=sQuery(id+"F24.wireOp",EDGE,"E105");var subQ2=makeQuery(id+"F25.opRevolve","SWEPT_EDGE",EDGE,{"disambiguationData":[OSD([subQ1,sQuery(id+"F24.wireOp",EDGE,"E106")])]});var subQ3=makeQuery(id+"F43.imprint","INTERSECT",VERTEX,{"derivedFrom":[subQ2,subQ0]});Q0=makeQuery(id+"F43.imprint","IMPRINT",FACE,{"disambiguationData":[TD([[makeQuery(id+"F43.imprint","IMPRINT",EDGE,{"disambiguationData":[TD([[subQ3,-1.0]])],"derivedFrom":subQ0}),1.0]])]});}
            var Q1;
            {var subQ0=sQuery(id+"F43.wireOp",EDGE,"E215");var subQ1=sQuery(id+"F24.wireOp",EDGE,"E105");var subQ2=makeQuery(id+"F25.opRevolve","SWEPT_EDGE",EDGE,{"disambiguationData":[OSD([subQ1,sQuery(id+"F24.wireOp",EDGE,"E106")])]});var subQ3=makeQuery(id+"F43.imprint","INTERSECT",VERTEX,{"derivedFrom":[subQ2,subQ0]});Q1=makeQuery(id+"F43.imprint","IMPRINT",FACE,{"disambiguationData":[TD([[makeQuery(id+"F43.imprint","IMPRINT",EDGE,{"disambiguationData":[TD([[subQ3,-1.0]])],"derivedFrom":subQ0}),-1.0]])]});}
            var Q2;
            {var subQ0=sQuery(id+"F43.wireOp",EDGE,"E216.17.0");var subQ1=sQuery(id+"F24.wireOp",EDGE,"E105");var subQ2=makeQuery(id+"F25.opRevolve","SWEPT_EDGE",EDGE,{"disambiguationData":[OSD([subQ1,sQuery(id+"F24.wireOp",EDGE,"E106")])]});var subQ3=makeQuery(id+"F43.imprint","INTERSECT",VERTEX,{"derivedFrom":[subQ2,subQ0]});Q2=makeQuery(id+"F43.imprint","IMPRINT",FACE,{"disambiguationData":[TD([[makeQuery(id+"F43.imprint","IMPRINT",EDGE,{"disambiguationData":[TD([[subQ3,-1.0]])],"derivedFrom":subQ0}),1.0]])]});}
            var Q3;
            {var subQ0=sQuery(id+"F43.wireOp",EDGE,"E216.15.0");var subQ1=sQuery(id+"F24.wireOp",EDGE,"E105");var subQ2=makeQuery(id+"F25.opRevolve","SWEPT_EDGE",EDGE,{"disambiguationData":[OSD([subQ1,sQuery(id+"F24.wireOp",EDGE,"E106")])]});var subQ3=makeQuery(id+"F43.imprint","INTERSECT",VERTEX,{"derivedFrom":[subQ2,subQ0]});Q3=makeQuery(id+"F43.imprint","IMPRINT",FACE,{"disambiguationData":[TD([[makeQuery(id+"F43.imprint","IMPRINT",EDGE,{"disambiguationData":[TD([[subQ3,-1.0]])],"derivedFrom":subQ0}),1.0]])]});}
            var Q4;
            {var subQ0=sQuery(id+"F43.wireOp",EDGE,"E216.13.0");var subQ1=sQuery(id+"F24.wireOp",EDGE,"E105");var subQ2=makeQuery(id+"F25.opRevolve","SWEPT_EDGE",EDGE,{"disambiguationData":[OSD([subQ1,sQuery(id+"F24.wireOp",EDGE,"E106")])]});var subQ3=makeQuery(id+"F43.imprint","INTERSECT",VERTEX,{"derivedFrom":[subQ2,subQ0]});Q4=makeQuery(id+"F43.imprint","IMPRINT",FACE,{"disambiguationData":[TD([[makeQuery(id+"F43.imprint","IMPRINT",EDGE,{"disambiguationData":[TD([[subQ3,-1.0]])],"derivedFrom":subQ0}),1.0]])]});}
            var Q5;
            {var subQ0=sQuery(id+"F43.wireOp",EDGE,"E216.11.0");var subQ1=sQuery(id+"F24.wireOp",EDGE,"E105");var subQ2=makeQuery(id+"F25.opRevolve","SWEPT_EDGE",EDGE,{"disambiguationData":[OSD([subQ1,sQuery(id+"F24.wireOp",EDGE,"E106")])]});var subQ3=makeQuery(id+"F43.imprint","INTERSECT",VERTEX,{"derivedFrom":[subQ2,subQ0]});Q5=makeQuery(id+"F43.imprint","IMPRINT",FACE,{"disambiguationData":[TD([[makeQuery(id+"F43.imprint","IMPRINT",EDGE,{"disambiguationData":[TD([[subQ3,-1.0]])],"derivedFrom":subQ0}),1.0]])]});}
            var Q6;
            {var subQ0=sQuery(id+"F43.wireOp",EDGE,"E216.9.0");var subQ1=sQuery(id+"F24.wireOp",EDGE,"E105");var subQ2=makeQuery(id+"F25.opRevolve","SWEPT_EDGE",EDGE,{"disambiguationData":[OSD([subQ1,sQuery(id+"F24.wireOp",EDGE,"E106")])]});var subQ3=makeQuery(id+"F43.imprint","INTERSECT",VERTEX,{"derivedFrom":[subQ2,subQ0]});Q6=makeQuery(id+"F43.imprint","IMPRINT",FACE,{"disambiguationData":[TD([[makeQuery(id+"F43.imprint","IMPRINT",EDGE,{"disambiguationData":[TD([[subQ3,-1.0]])],"derivedFrom":subQ0}),1.0]])]});}
            var Q7;
            {var subQ0=sQuery(id+"F43.wireOp",EDGE,"E216.7.0");var subQ1=sQuery(id+"F24.wireOp",EDGE,"E105");var subQ2=makeQuery(id+"F25.opRevolve","SWEPT_EDGE",EDGE,{"disambiguationData":[OSD([subQ1,sQuery(id+"F24.wireOp",EDGE,"E106")])]});var subQ3=makeQuery(id+"F43.imprint","INTERSECT",VERTEX,{"derivedFrom":[subQ2,subQ0]});Q7=makeQuery(id+"F43.imprint","IMPRINT",FACE,{"disambiguationData":[TD([[makeQuery(id+"F43.imprint","IMPRINT",EDGE,{"disambiguationData":[TD([[subQ3,-1.0]])],"derivedFrom":subQ0}),1.0]])]});}
            var Q8;
            {var subQ0=sQuery(id+"F43.wireOp",EDGE,"E216.5.0");var subQ1=sQuery(id+"F24.wireOp",EDGE,"E105");var subQ2=makeQuery(id+"F25.opRevolve","SWEPT_EDGE",EDGE,{"disambiguationData":[OSD([subQ1,sQuery(id+"F24.wireOp",EDGE,"E106")])]});var subQ3=makeQuery(id+"F43.imprint","INTERSECT",VERTEX,{"derivedFrom":[subQ2,subQ0]});Q8=makeQuery(id+"F43.imprint","IMPRINT",FACE,{"disambiguationData":[TD([[makeQuery(id+"F43.imprint","IMPRINT",EDGE,{"disambiguationData":[TD([[subQ3,-1.0]])],"derivedFrom":subQ0}),1.0]])]});}
            var Q9;
            {var subQ0=sQuery(id+"F43.wireOp",EDGE,"E216.3.0");var subQ1=sQuery(id+"F24.wireOp",EDGE,"E105");var subQ2=makeQuery(id+"F25.opRevolve","SWEPT_EDGE",EDGE,{"disambiguationData":[OSD([subQ1,sQuery(id+"F24.wireOp",EDGE,"E106")])]});var subQ3=makeQuery(id+"F43.imprint","INTERSECT",VERTEX,{"derivedFrom":[subQ2,subQ0]});Q9=makeQuery(id+"F43.imprint","IMPRINT",FACE,{"disambiguationData":[TD([[makeQuery(id+"F43.imprint","IMPRINT",EDGE,{"disambiguationData":[TD([[subQ3,-1.0]])],"derivedFrom":subQ0}),1.0]])]});}
            extrude(context, id + "F45", {"entities" : qUnion([Q0, Q1, Q2, Q3, Q4, Q5, Q6, Q7, Q8, Q9]), "operationType" : NewBodyOperationType.REMOVE, "oppositeDirection" : true, "depth" : 3 * mm, "offsetDistance" : 25 * mm, "hasDraft" : true, "draftAngle" : 45 * degree, "draftPullDirection" : true});
        }
        {
            var Q0;
            Q0=makeQuery(id+"F29.imprint","IMPRINT",FACE,{"disambiguationData":[TD([[makeQuery(id+"F29.imprint","IMPRINT",EDGE,{"derivedFrom":sQuery(id+"F29.wireOp",EDGE,"E137")}),-1.0]])]});
            var Q1;
            Q1=makeQuery(id+"F29.imprint","IMPRINT",FACE,{"disambiguationData":[TD([[makeQuery(id+"F29.imprint","IMPRINT",EDGE,{"derivedFrom":sQuery(id+"F29.wireOp",EDGE,"E135")}),-1.0]])]});
            var Q2;
            Q2=makeQuery(id+"F29.imprint","IMPRINT",FACE,{"disambiguationData":[TD([[makeQuery(id+"F29.imprint","IMPRINT",EDGE,{"derivedFrom":sQuery(id+"F29.wireOp",EDGE,"E138")}),1.0]])]});
            extrude(context, id + "F46", {"entities" : qUnion([Q0, Q1, Q2]), "operationType" : NewBodyOperationType.REMOVE, "oppositeDirection" : true, "depth" : 5 * mm, "offsetDistance" : 25 * mm, "hasDraft" : true, "draftAngle" : 45 * degree, "draftPullDirection" : true});
        }
        {
            var Q0;
            Q0=makeQuery(id+"F36.boolean.opBoolean","SPLIT",FACE,{"disambiguationData":[TD([makeQuery(id+"F18.opRevolve","SWEPT_FACE",FACE,{"disambiguationData":[OSD([sQuery(id+"F17.wireOp",EDGE,"E14")])]})])],"derivedFrom":makeQuery(id+"F18.opRevolve","SWEPT_FACE",FACE,{"disambiguationData":[OSD([sQuery(id+"F17.wireOp",EDGE,"E13")])]})});
            var sketch = newSketch(context, id + "F47", { "sketchPlane" : qUnion([Q0])});
            skCircle(sketch, "E238", {"center": v(0, 0) * mm, "radius": 25.31 * mm});
            skCircle(sketch, "E239", {"center": v(0, 0) * mm, "radius": 29.93 * mm});
            skCircle(sketch, "E240", {"center": v(0, 0) * mm, "radius": 35.5 * mm});
            skCircle(sketch, "E241", {"center": v(0, 0) * mm, "radius": 20.2 * mm});
            skSolve(sketch);
        }
        {
            var Q0;
            Q0=makeQuery(id+"F47.imprint","IMPRINT",FACE,{"disambiguationData":[TD([[makeQuery(id+"F47.imprint","IMPRINT",EDGE,{"derivedFrom":sQuery(id+"F47.wireOp",EDGE,"E238")}),1.0]])]});
            var Q1;
            Q1=makeQuery(id+"F47.imprint","IMPRINT",FACE,{"disambiguationData":[TD([[makeQuery(id+"F47.imprint","IMPRINT",EDGE,{"derivedFrom":sQuery(id+"F47.wireOp",EDGE,"E239")}),-1.0]])]});
            extrude(context, id + "F48", {"entities" : qUnion([Q0, Q1]), "operationType" : NewBodyOperationType.REMOVE, "oppositeDirection" : true, "depth" : 5 * mm, "offsetDistance" : 25 * mm, "hasDraft" : true, "draftAngle" : 45 * degree, "draftPullDirection" : true});
        }
        {
            var Q0;
            Q0=makeQuery(id+"F30.imprint","IMPRINT",FACE,{"disambiguationData":[TD([[makeQuery(id+"F30.imprint","IMPRINT",EDGE,{"derivedFrom":sQuery(id+"F30.wireOp",EDGE,"E139")}),-1.0]])]});
            var Q1;
            Q1=makeQuery(id+"F30.imprint","IMPRINT",FACE,{"disambiguationData":[TD([[makeQuery(id+"F30.imprint","IMPRINT",EDGE,{"derivedFrom":sQuery(id+"F30.wireOp",EDGE,"E140")}),-1.0]])]});
            var Q2;
            Q2=makeQuery(id+"F30.imprint","IMPRINT",FACE,{"disambiguationData":[TD([[makeQuery(id+"F30.imprint","IMPRINT",EDGE,{"derivedFrom":sQuery(id+"F30.wireOp",EDGE,"E141")}),1.0]])]});
            extrude(context, id + "F49", {"entities" : qUnion([Q0, Q1, Q2]), "operationType" : NewBodyOperationType.REMOVE, "oppositeDirection" : true, "depth" : 25 * mm, "offsetDistance" : 25 * mm, "hasDraft" : true, "draftAngle" : 45 * degree, "draftPullDirection" : true});
        }
        {
            var Q0;
            Q0=makeQuery(id+"F31.imprint","IMPRINT",FACE,{"disambiguationData":[TD([[makeQuery(id+"F31.imprint","IMPRINT",EDGE,{"derivedFrom":sQuery(id+"F31.wireOp",EDGE,"E143")}),1.0]])]});
            var Q1;
            Q1=makeQuery(id+"F31.imprint","IMPRINT",FACE,{"disambiguationData":[TD([[makeQuery(id+"F31.imprint","IMPRINT",EDGE,{"derivedFrom":sQuery(id+"F31.wireOp",EDGE,"E144")}),-1.0]])]});
            var Q2;
            Q2=makeQuery(id+"F31.imprint","IMPRINT",FACE,{"disambiguationData":[TD([[makeQuery(id+"F31.imprint","IMPRINT",EDGE,{"derivedFrom":sQuery(id+"F31.wireOp",EDGE,"E145")}),1.0]])]});
            extrude(context, id + "F50", {"entities" : qUnion([Q0, Q1, Q2]), "operationType" : NewBodyOperationType.REMOVE, "oppositeDirection" : true, "depth" : 25 * mm, "offsetDistance" : 25 * mm, "hasDraft" : true, "draftAngle" : 45 * degree, "draftPullDirection" : true});
        }
        {
            var Q0;
            Q0=makeQuery(id+"F27.imprint","IMPRINT",FACE,{"disambiguationData":[TD([[makeQuery(id+"F27.imprint","IMPRINT",EDGE,{"derivedFrom":sQuery(id+"F27.wireOp",EDGE,"E109")}),1.0]])]});
            var Q1;
            Q1=makeQuery(id+"F27.imprint","IMPRINT",FACE,{"disambiguationData":[TD([[makeQuery(id+"F27.imprint","IMPRINT",EDGE,{"derivedFrom":sQuery(id+"F27.wireOp",EDGE,"E110")}),-1.0]])]});
            var Q2;
            Q2=makeQuery(id+"F27.imprint","IMPRINT",FACE,{"disambiguationData":[TD([[makeQuery(id+"F27.imprint","IMPRINT",EDGE,{"derivedFrom":sQuery(id+"F27.wireOp",EDGE,"E111")}),1.0]])]});
            extrude(context, id + "F51", {"entities" : qUnion([Q0, Q1, Q2]), "operationType" : NewBodyOperationType.REMOVE, "oppositeDirection" : true, "depth" : 5 * mm, "offsetDistance" : 25 * mm, "hasDraft" : true, "draftAngle" : 45 * degree, "draftPullDirection" : true});
        }
        {
            var Q0;
            Q0=makeQuery(id+"F0.imprint","IMPRINT",FACE,{"disambiguationData":[TD([[makeQuery(id+"F0.imprint","IMPRINT",EDGE,{"derivedFrom":sQuery(id+"F0.wireOp",EDGE,"E0.bottom")}),-1.0]])]});
            var sketch = newSketch(context, id + "F52", { "sketchPlane" : qUnion([Q0])});
            skCircle(sketch, "E242.cCircle", {"center": v(38, 0) * mm, "radius": 1.5 * mm, "construction": true});
            skLineSegment(sketch, "E242.0", {"start": v(39.5, 2.6) * mm, "end": v(39.5, -2.6) * mm});
            skLineSegment(sketch, "E242.1", {"start": v(39.5, -2.6) * mm, "end": v(35, 0) * mm});
            skLineSegment(sketch, "E242.2", {"start": v(35, 0) * mm, "end": v(39.5, 2.6) * mm});
            skPoint(sketch, "E242.0.midPoint", {"position": v(39.5, 0) * mm});
            skSolve(sketch);
        }
        {
            var Q0;
            Q0 = qSketchRegion(id + "F52", true);
            extrude(context, id + "F53", {"entities" : qUnion([Q0]), "operationType" : NewBodyOperationType.REMOVE, "oppositeDirection" : true, "depth" : 1 * mm, "offsetDistance" : 25 * mm});
        }
    });
